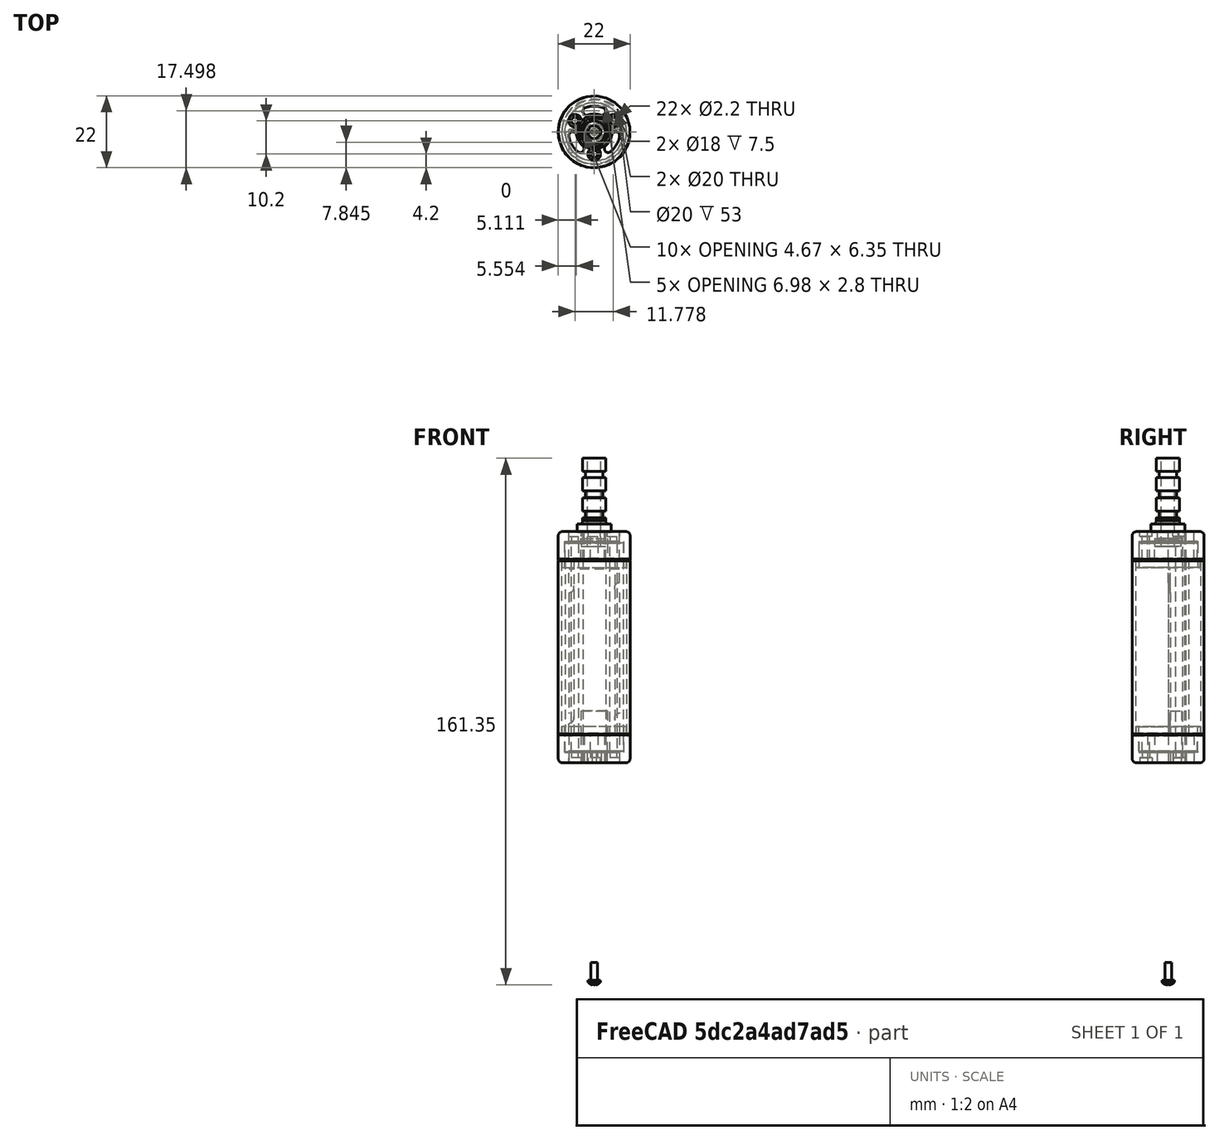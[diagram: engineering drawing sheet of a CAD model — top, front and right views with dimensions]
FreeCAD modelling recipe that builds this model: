
FCSTD DOCUMENT  (FreeCAD 1.1R44227 +568 (Git))
Label: Enclosure
License: All rights reserved
LicenseURL: http://en.wikipedia.org/wiki/All_rights_reserved
objects: Sketcher::SketchObject×40, PartDesign::Pocket×28, PartDesign::Pad×16, App::Point×15, PartDesign::Body×14, PartDesign::Fillet×12, App::FeaturePython×12, PartDesign::SubShapeBinder×9, App::Link×6, PartDesign::Plane×2, PartDesign::Revolution×2, Assembly::JointGroup×1, Assembly::ViewGroup×1, Assembly::AssemblyObject×1
note: 279 computed .brp shape members not serialized (recipe doc carries the construction recipe); baked Part::Feature solids carry a one-line shape summary decoded from their .brp

FEATURE [Sketcher::SketchObject] Sketch  label="22mmCircle"
  ArcFitTolerance = 1e-06
  AttachmentSupport = -> [XY_Plane]
  ExternalTypes = [0]
  FullyConstrained = true
  MakeInternals = false
  MapMode = 5
  _ExternalGeoVersion = 0
  sketch-geometry (1):
    g0: Circle CenterX=0 CenterY=0 CenterZ=0 NormalX=0 NormalY=0 NormalZ=1 AngleXU=0 Radius=11
  constraints (2):
    c: Diameter(g0) = 22
    c: Coincident(g0,g-1)
FEATURE [PartDesign::Pad] Pad
  Direction = (0,0,1)
  Length = 8.5
  Length2 = 10
  Profile = -> Sketch
  ReferenceAxis = -> Sketch [N_Axis]
  SideType = 0
  Suppressed = false
  Type = 0
  Type2 = 0
FEATURE [Sketcher::SketchObject] Sketch001
  ArcFitTolerance = 1e-06
  AttachmentSupport = -> [Pad]
  ExternalTypes = [0]
  FullyConstrained = true
  MakeInternals = false
  MapMode = 5
  Placement = pos=(0,0,8.5) rot=(0,0,1;0rad)
  _ExternalGeoVersion = 0
  sketch-geometry (1):
    g0: Circle CenterX=0 CenterY=0 CenterZ=0 NormalX=0 NormalY=0 NormalZ=1 AngleXU=0 Radius=9.85
  constraints (2):
    c: Diameter(g0) = 19.7
    c: Coincident(g0,g-1)
FEATURE [PartDesign::Pad] Pad001
  BaseFeature = -> Pad
  Direction = (0,0,1)
  Length = 2.5
  Length2 = 10
  Profile = -> Sketch001
  ReferenceAxis = -> Sketch001 [N_Axis]
  SideType = 0
  Suppressed = false
  Type = 0
  Type2 = 0
FEATURE [Sketcher::SketchObject] Sketch002
  ArcFitTolerance = 1e-06
  AttachmentSupport = -> [Pad001]
  ExternalTypes = [0]
  FullyConstrained = true
  MakeInternals = false
  MapMode = 5
  Placement = pos=(0,0,11) rot=(0,0,1;0rad)
  _ExternalGeoVersion = 0
  sketch-geometry (1):
    g0: Circle CenterX=0 CenterY=0 CenterZ=0 NormalX=0 NormalY=0 NormalZ=1 AngleXU=0 Radius=9
  constraints (2):
    c: Diameter(g0) = 18
    c: Coincident(g0,g-1)
FEATURE [PartDesign::Pocket] Pocket
  BaseFeature = -> Pad001
  Direction = (0,0,-1)
  Length = 7.5
  Length2 = 5
  Profile = -> Sketch002
  ReferenceAxis = -> Sketch002 [N_Axis]
  SideType = 0
  Suppressed = false
  Type = 0
  Type2 = 0
FEATURE [Sketcher::SketchObject] Sketch003  label="BoltHoles_outer"
  ArcFitTolerance = 1e-06
  AttachmentSupport = -> [Pocket]
  ExternalGeometry = -> [Pocket]
  ExternalTypes = [0]
  FullyConstrained = true
  MakeInternals = false
  MapMode = 5
  Placement = pos=(0,0,0) rot=(1,0,0;3.14159rad)
  _ExternalGeoVersion = 0
  sketch-geometry (5):
    g0: Circle CenterX=0 CenterY=6.8 CenterZ=0 NormalX=0 NormalY=0 NormalZ=1 AngleXU=0 Radius=1.95
    g1: Circle CenterX=-5.88897 CenterY=-3.4 CenterZ=0 NormalX=0 NormalY=0 NormalZ=1 AngleXU=0 Radius=1.95
    g2: Circle CenterX=5.88897 CenterY=-3.4 CenterZ=0 NormalX=0 NormalY=0 NormalZ=1 AngleXU=0 Radius=1.95
    g3: LineSegment [constr] StartX=0 StartY=0 StartZ=0 EndX=5.88897 EndY=-3.4 EndZ=0
    g4: LineSegment [constr] StartX=-5.88897 StartY=-3.4 StartZ=0 EndX=0 EndY=0 EndZ=0
  constraints (13):
    c: Diameter(g0) = 3.9
    c: PointOnObject(g0,g-2)
    c: Diameter(g1) = 3.9
    c: Diameter(g2) = 3.9
    c: Distance(g-1,g0) = 6.8
    c: Distance(g-1,g1) = 6.8
    c: Distance(g-1,g2) = 6.8
    c: Coincident(g3,g-1)
    c: Coincident(g3,g2)
    c: Angle(g3,g-2) = 2.0944
    c: Coincident(g4,g1)
    c: Coincident(g4,g3)
    c: Angle(g-2,g4) = 2.0944
FEATURE [PartDesign::Pocket] Pocket001
  BaseFeature = -> Pocket
  Direction = (0,0,1)
  Length = 1.5
  Length2 = 5
  Profile = -> Sketch003
  ReferenceAxis = -> Sketch003 [N_Axis]
  SideType = 0
  Suppressed = false
  Type = 0
  Type2 = 0
FEATURE [PartDesign::Fillet] Fillet
  Base = -> Pocket001 [Edge2]
  BaseFeature = -> Pocket001
  Radius = 1.2
  SupportTransform = false
  Suppressed = false
  UseAllEdges = false
FEATURE [Sketcher::SketchObject] Sketch005  label="BoltHoles_inner"
  ArcFitTolerance = 1e-06
  AttachmentSupport = -> [Fillet]
  ExternalGeometry = -> [Fillet]
  ExternalTypes = [0]
  FullyConstrained = true
  MakeInternals = false
  MapMode = 5
  Placement = pos=(0,0,1.5) rot=(1,0,0;3.14159rad)
  _ExternalGeoVersion = 0
  sketch-geometry (3):
    g0: Circle CenterX=-5.88897 CenterY=-3.4 CenterZ=0 NormalX=0 NormalY=0 NormalZ=1 AngleXU=0 Radius=1.1
    g1: Circle CenterX=0 CenterY=6.8 CenterZ=0 NormalX=0 NormalY=0 NormalZ=1 AngleXU=0 Radius=1.1
    g2: Circle CenterX=5.88897 CenterY=-3.4 CenterZ=0 NormalX=0 NormalY=0 NormalZ=1 AngleXU=0 Radius=1.1
  constraints (6):
    c: Diameter(g0) = 2.2
    c: Coincident(g0,g-4)
    c: Diameter(g1) = 2.2
    c: Coincident(g1,g-3)
    c: Diameter(g2) = 2.2
    c: Coincident(g2,g-5)
FEATURE [PartDesign::Pocket] Pocket002
  BaseFeature = -> Fillet
  Direction = (0,0,1)
  Length = 2
  Length2 = 5
  Profile = -> Sketch005
  ReferenceAxis = -> Sketch005 [N_Axis]
  SideType = 0
  Suppressed = false
  Type = 0
  Type2 = 0
FEATURE [Sketcher::SketchObject] Sketch006
  ArcFitTolerance = 1e-06
  AttachmentSupport = -> [XY_Plane001]
  ExternalTypes = [0]
  FullyConstrained = true
  MakeInternals = false
  MapMode = 5
  _ExternalGeoVersion = 0
  sketch-geometry (2):
    g0: Circle CenterX=0 CenterY=0 CenterZ=0 NormalX=0 NormalY=0 NormalZ=1 AngleXU=0 Radius=11
    g1: Circle CenterX=0 CenterY=0 CenterZ=0 NormalX=0 NormalY=0 NormalZ=1 AngleXU=0 Radius=10
  constraints (4):
    c: Diameter(g0) = 22
    c: Coincident(g0,g-1)
    c: Diameter(g1) = 20
    c: Coincident(g1,g0)
FEATURE [PartDesign::Pad] Pad002
  Direction = (0,0,1)
  Length = 53
  Length2 = 10
  Profile = -> Sketch006
  ReferenceAxis = -> Sketch006 [N_Axis]
  SideType = 0
  Suppressed = false
  Type = 0
  Type2 = 0
FEATURE [PartDesign::Body] Body001  label="QuartzTube"
  AllowCompound = false
  Group = -> [Sketch006,Pad002]
  Origin = -> Origin001
  Placement = pos=(0,0,77) rot=(0,0,1;0rad)
  Tip = -> Pad002
FEATURE [Sketcher::SketchObject] Sketch007  label="VentHoles"
  ArcFitTolerance = 1e-06
  AttachmentSupport = -> [Pocket002]
  ExternalGeometry = -> [Pocket002]
  ExternalTypes = [0]
  FullyConstrained = true
  MakeInternals = false
  MapMode = 5
  Placement = pos=(0,0,0) rot=(1,0,0;3.14159rad)
  _ExternalGeoVersion = 0
  sketch-geometry (58):
    g0: Circle [constr] CenterX=0 CenterY=0 CenterZ=0 NormalX=0 NormalY=0 NormalZ=1 AngleXU=0 Radius=7.9
    g1: Circle [constr] CenterX=0 CenterY=0 CenterZ=0 NormalX=0 NormalY=0 NormalZ=1 AngleXU=0 Radius=5.5
    g2: Circle [constr] CenterX=0 CenterY=0 CenterZ=0 NormalX=0 NormalY=0 NormalZ=1 AngleXU=0 Radius=4
    g3: Circle [constr] CenterX=0 CenterY=0 CenterZ=0 NormalX=0 NormalY=0 NormalZ=1 AngleXU=0 Radius=1.6
    g4: LineSegment [constr] StartX=0 StartY=0 StartZ=0 EndX=-6.29932 EndY=7.50724 EndZ=0
    g5: LineSegment [constr] StartX=0 StartY=0 StartZ=0 EndX=-9.65112 EndY=1.70175 EndZ=0
    g6: GeomPoint X=-5.07802 Y=6.05175 Z=0
    g7: GeomPoint X=-3.53533 Y=4.21324 Z=0
    g8: ArcOfCircle CenterX=-4.30668 CenterY=5.1325 CenterZ=0 NormalX=0 NormalY=0 NormalZ=1 AngleXU=0 Radius=1.2 StartAngle=5.41052 EndAngle=8.55211
    g9: GeomPoint X=-7.77998 Y=1.37182 Z=0
    g10: GeomPoint X=-5.41644 Y=0.955065 Z=0
    g11: ArcOfCircle CenterX=-6.59821 CenterY=1.16344 CenterZ=0 NormalX=0 NormalY=0 NormalZ=1 AngleXU=0 Radius=1.2 StartAngle=2.96706 EndAngle=6.10865
    g12: ArcOfCircle CenterX=0 CenterY=0 CenterZ=0 NormalX=0 NormalY=0 NormalZ=1 AngleXU=0 Radius=7.9 StartAngle=2.26893 EndAngle=2.96706
    g13: ArcOfCircle CenterX=-3e-16 CenterY=1e-16 CenterZ=0 NormalX=0 NormalY=0 NormalZ=1 AngleXU=0 Radius=5.5 StartAngle=2.26893 EndAngle=2.96706
    g14: LineSegment [constr] StartX=0 StartY=0 StartZ=0 EndX=6.29932 EndY=7.50724 EndZ=0
    g15: LineSegment [constr] StartX=-3e-16 StartY=1e-16 StartZ=0 EndX=9.65112 EndY=1.70175 EndZ=0
    g16: LineSegment [constr] StartX=0 StartY=0 StartZ=0 EndX=3.3518 EndY=-9.20899 EndZ=0
    g17: LineSegment [constr] StartX=0 StartY=0 StartZ=0 EndX=-3.3518 EndY=-9.20899 EndZ=0
    g18: GeomPoint X=5.07802 Y=6.05175 Z=0
    g19: GeomPoint X=3.53533 Y=4.21324 Z=0
    g20: GeomPoint X=5.41644 Y=0.955065 Z=0
    g21: GeomPoint X=7.77998 Y=1.37182 Z=0
    g22: GeomPoint X=-1.88111 Y=-5.16831 Z=0
    g23: GeomPoint X=-2.70196 Y=-7.42357 Z=0
    g24: GeomPoint X=1.88111 Y=-5.16831 Z=0
    g25: GeomPoint X=2.70196 Y=-7.42357 Z=0
    g26: ArcOfCircle CenterX=4.30668 CenterY=5.1325 CenterZ=0 NormalX=0 NormalY=0 NormalZ=1 AngleXU=0 Radius=1.2 StartAngle=0.872665 EndAngle=4.01426
    g27: ArcOfCircle CenterX=6.59821 CenterY=1.16344 CenterZ=0 NormalX=0 NormalY=0 NormalZ=1 AngleXU=0 Radius=1.2 StartAngle=3.31613 EndAngle=6.45772
    g28: ArcOfCircle CenterX=-3e-16 CenterY=0 CenterZ=0 NormalX=0 NormalY=0 NormalZ=1 AngleXU=0 Radius=7.9 StartAngle=0.174533 EndAngle=0.872665
    g29: ArcOfCircle CenterX=-1e-16 CenterY=9e-16 CenterZ=0 NormalX=0 NormalY=0 NormalZ=1 AngleXU=0 Radius=5.5 StartAngle=0.174533 EndAngle=0.872665
    g30: ArcOfCircle CenterX=-2.29153 CenterY=-6.29594 CenterZ=0 NormalX=0 NormalY=0 NormalZ=1 AngleXU=0 Radius=1.2 StartAngle=1.22173 EndAngle=4.36332
    g31: ArcOfCircle CenterX=2.29153 CenterY=-6.29594 CenterZ=0 NormalX=0 NormalY=0 NormalZ=1 AngleXU=0 Radius=1.2 StartAngle=5.06145 EndAngle=8.20305
    g32: ArcOfCircle CenterX=-1.5e-15 CenterY=2e-16 CenterZ=0 NormalX=0 NormalY=0 NormalZ=1 AngleXU=0 Radius=7.9 StartAngle=4.36332 EndAngle=5.06145
    g33: ArcOfCircle CenterX=-2e-16 CenterY=-2e-16 CenterZ=0 NormalX=0 NormalY=0 NormalZ=1 AngleXU=0 Radius=5.5 StartAngle=4.36332 EndAngle=5.06145
    g34: GeomPoint X=-2.57115 Y=3.06418 Z=0
    g35: GeomPoint X=-1.02846 Y=1.22567 Z=0
    g36: GeomPoint X=-3.93923 Y=0.694593 Z=0
    g37: GeomPoint X=-1.57569 Y=0.277837 Z=0
    g38: ArcOfCircle CenterX=-1.79981 CenterY=2.14492 CenterZ=0 NormalX=0 NormalY=0 NormalZ=1 AngleXU=0 Radius=1.2 StartAngle=5.41052 EndAngle=8.55211
    g39: ArcOfCircle CenterX=-2.75746 CenterY=0.486215 CenterZ=0 NormalX=0 NormalY=0 NormalZ=1 AngleXU=0 Radius=1.2 StartAngle=2.96706 EndAngle=6.10865
    g40: ArcOfCircle CenterX=-6e-16 CenterY=-4e-16 CenterZ=0 NormalX=0 NormalY=0 NormalZ=1 AngleXU=0 Radius=4 StartAngle=2.26893 EndAngle=2.96706
    g41: ArcOfCircle CenterX=1e-16 CenterY=1e-16 CenterZ=0 NormalX=0 NormalY=0 NormalZ=1 AngleXU=0 Radius=1.6 StartAngle=2.26893 EndAngle=2.96706
    g42: GeomPoint X=1.02846 Y=1.22567 Z=0
    g43: GeomPoint X=2.57115 Y=3.06418 Z=0
    g44: GeomPoint X=1.57569 Y=0.277837 Z=0
    g45: GeomPoint X=3.93923 Y=0.694593 Z=0
    g46: GeomPoint X=1.36808 Y=-3.75877 Z=0
    g47: GeomPoint X=0.547232 Y=-1.50351 Z=0
    g48: GeomPoint X=-1.36808 Y=-3.75877 Z=0
    g49: GeomPoint X=-0.547232 Y=-1.50351 Z=0
    g50: ArcOfCircle CenterX=0 CenterY=0 CenterZ=0 NormalX=0 NormalY=0 NormalZ=1 AngleXU=0 Radius=1.6 StartAngle=4.36332 EndAngle=5.06145
    g51: ArcOfCircle CenterX=-3e-16 CenterY=-4e-16 CenterZ=0 NormalX=0 NormalY=0 NormalZ=1 AngleXU=0 Radius=4 StartAngle=4.36332 EndAngle=5.06145
    g52: ArcOfCircle CenterX=0.957656 CenterY=-2.63114 CenterZ=0 NormalX=0 NormalY=0 NormalZ=1 AngleXU=0 Radius=1.2 StartAngle=5.06145 EndAngle=8.20305
    g53: ArcOfCircle CenterX=-0.957656 CenterY=-2.63114 CenterZ=0 NormalX=0 NormalY=0 NormalZ=1 AngleXU=0 Radius=1.2 StartAngle=1.22173 EndAngle=4.36332
    g54: ArcOfCircle CenterX=1.79981 CenterY=2.14492 CenterZ=0 NormalX=0 NormalY=0 NormalZ=1 AngleXU=0 Radius=1.2 StartAngle=0.872665 EndAngle=4.01426
    g55: ArcOfCircle CenterX=2.75746 CenterY=0.486215 CenterZ=0 NormalX=0 NormalY=0 NormalZ=1 AngleXU=0 Radius=1.2 StartAngle=3.31613 EndAngle=6.45772
    g56: ArcOfCircle CenterX=1e-16 CenterY=1e-16 CenterZ=0 NormalX=0 NormalY=0 NormalZ=1 AngleXU=0 Radius=1.6 StartAngle=0.174533 EndAngle=0.872665
    g57: ArcOfCircle CenterX=-1.6749e-12 CenterY=-9.675e-13 CenterZ=0 NormalX=0 NormalY=0 NormalZ=1 AngleXU=0 Radius=4 StartAngle=0.174533 EndAngle=0.872665
  constraints (146):
    c: Diameter(g0) = 15.8
    c: Coincident(g0,g-1)
    c: Diameter(g1) = 11
    c: Coincident(g1,g0)
    c: Diameter(g2) = 8
    c: Coincident(g2,g0)
    c: Diameter(g3) = 3.2
    c: Coincident(g3,g0)
    c: Coincident(g4,g0)
    c: PointOnObject(g4,g-3)
    c: Angle(g-2,g4) = 0.698132
    c: Coincident(g5,g0)
    c: PointOnObject(g5,g-3)
    c: Angle(g4,g5) = 0.698132
    c: PointOnObject(g6,g0)
    c: PointOnObject(g6,g4)
    c: PointOnObject(g7,g1)
    c: PointOnObject(g7,g4)
    c: Coincident(g8,g6)
    c: Coincident(g8,g7)
    c: PointOnObject(g8,g4)
    c: PointOnObject(g9,g0)
    c: PointOnObject(g10,g1)
    c: PointOnObject(g10,g5)
    c: PointOnObject(g9,g5)
    c: Coincident(g11,g9)
    c: Coincident(g11,g10)
    c: PointOnObject(g11,g5)
    c: Equal(g0,g12)
    c: Coincident(g12,g6)
    c: Coincident(g12,g9)
    c: Equal(g13,g1)
    c: Coincident(g13,g7)
    c: Coincident(g13,g10)
    c: Coincident(g14,g12)
    c: PointOnObject(g14,g-3)
    c: Coincident(g15,g13)
    c: PointOnObject(g15,g-3)
    c: Angle(g14,g-2) = 0.698132
    c: Angle(g15,g14) = 0.698132
    c: Coincident(g16,g0)
    c: PointOnObject(g16,g-3)
    c: Coincident(g17,g0)
    c: PointOnObject(g17,g-3)
    c: Angle(g-2,g16) = 0.349066
    c: Angle(g17,g16) = 0.698132
    c: PointOnObject(g18,g14)
    c: PointOnObject(g19,g14)
    c: PointOnObject(g20,g15)
    c: PointOnObject(g21,g15)
    c: PointOnObject(g18,g0)
    c: PointOnObject(g19,g1)
    c: PointOnObject(g20,g1)
    c: PointOnObject(g21,g0)
    c: PointOnObject(g22,g17)
    c: PointOnObject(g23,g17)
    c: PointOnObject(g24,g16)
    c: PointOnObject(g25,g16)
    c: PointOnObject(g25,g0)
    c: PointOnObject(g24,g1)
    c: PointOnObject(g22,g1)
    c: PointOnObject(g23,g0)
    c: Coincident(g26,g18)
    c: Coincident(g26,g19)
    c: Coincident(g27,g20)
    c: Coincident(g27,g21)
    c: PointOnObject(g27,g15)
    c: PointOnObject(g26,g14)
    c: Coincident(g28,g18)
    c: Coincident(g28,g21)
    c: Equal(g0,g28)
    c: Coincident(g29,g19)
    c: Coincident(g29,g20)
    c: Equal(g29,g1)
    c: Coincident(g30,g22)
    c: Coincident(g30,g23)
    c: Coincident(g31,g25)
    c: Coincident(g31,g24)
    c: PointOnObject(g31,g16)
    c: PointOnObject(g30,g17)
    c: Coincident(g33,g24)
    c: Coincident(g33,g22)
    c: Coincident(g32,g23)
    c: Coincident(g32,g25)
    c: Equal(g33,g1)
    c: Equal(g32,g0)
    c: PointOnObject(g34,g4)
    c: PointOnObject(g35,g4)
    c: PointOnObject(g36,g5)
    c: PointOnObject(g37,g5)
    c: PointOnObject(g34,g2)
    c: PointOnObject(g35,g3)
    c: PointOnObject(g37,g3)
    c: PointOnObject(g36,g2)
    c: Coincident(g38,g35)
    c: Coincident(g38,g34)
    c: Coincident(g39,g37)
    c: Coincident(g39,g36)
    c: PointOnObject(g39,g5)
    c: PointOnObject(g38,g4)
    c: Coincident(g41,g35)
    c: Coincident(g41,g37)
    c: Coincident(g40,g34)
    c: Coincident(g40,g36)
    c: Equal(g40,g2)
    c: Equal(g41,g3)
    c: PointOnObject(g42,g14)
    c: PointOnObject(g43,g14)
    c: PointOnObject(g44,g15)
    c: PointOnObject(g45,g15)
    c: PointOnObject(g46,g16)
    c: PointOnObject(g47,g16)
    c: PointOnObject(g48,g17)
    c: PointOnObject(g49,g17)
    c: PointOnObject(g47,g3)
    c: PointOnObject(g46,g2)
    c: PointOnObject(g48,g2)
    c: PointOnObject(g49,g3)
    c: PointOnObject(g45,g2)
    c: PointOnObject(g43,g2)
    c: PointOnObject(g42,g3)
    c: PointOnObject(g44,g3)
    c: Coincident(g51,g46)
    c: Coincident(g51,g48)
    c: Coincident(g50,g49)
    c: Coincident(g47,g50)
    c: Equal(g51,g2)
    c: Equal(g50,g3)
    c: Coincident(g52,g47)
    c: Coincident(g52,g46)
    c: Coincident(g53,g48)
    c: Coincident(g53,g49)
    c: PointOnObject(g53,g17)
    c: PointOnObject(g52,g16)
    c: Coincident(g54,g42)
    c: Coincident(g54,g43)
    c: Coincident(g55,g44)
    c: Coincident(g55,g45)
    c: PointOnObject(g55,g15)
    c: PointOnObject(g54,g14)
    c: Coincident(g42,g56)
    c: Coincident(g56,g44)
    c: Coincident(g57,g43)
    c: Coincident(g57,g45)
    c: Equal(g56,g3)
    c: Equal(g57,g2)
FEATURE [PartDesign::Pocket] Pocket003
  BaseFeature = -> Pocket002
  Direction = (0,0,1)
  Length = 3.5
  Length2 = 5
  Profile = -> Sketch007
  ReferenceAxis = -> Sketch007 [N_Axis]
  SideType = 0
  Suppressed = false
  Type = 0
  Type2 = 0
FEATURE [PartDesign::Body] Body  label="EndCap_Bottom"
  AllowCompound = false
  Group = -> [Sketch,Pad,Sketch001,Pad001,Sketch002,Pocket,Sketch003,Pocket001,Fillet,Sketch005,Pocket002,Sketch007,Pocket003]
  Origin = -> Origin
  Placement = pos=(0,1e-05,68.2) rot=(0,0,1;0rad)
  Tip = -> Pocket003
FEATURE [Sketcher::SketchObject] Sketch008  label="22mmCircle001"
  ArcFitTolerance = 1e-06
  AttachmentSupport = -> [XY_Plane002]
  ExternalTypes = [0]
  FullyConstrained = true
  MakeInternals = false
  MapMode = 5
  _ExternalGeoVersion = 0
  sketch-geometry (1):
    g0: Circle CenterX=0 CenterY=0 CenterZ=0 NormalX=0 NormalY=0 NormalZ=1 AngleXU=0 Radius=11
  constraints (2):
    c: Diameter(g0) = 22
    c: Coincident(g0,g-1)
FEATURE [PartDesign::Pad] Pad003
  Direction = (0,0,1)
  Length = 8.5
  Length2 = 10
  Profile = -> Sketch008
  ReferenceAxis = -> Sketch008 [N_Axis]
  SideType = 0
  Suppressed = false
  Type = 0
  Type2 = 0
FEATURE [Sketcher::SketchObject] Sketch009
  ArcFitTolerance = 1e-06
  AttachmentSupport = -> [Pad003]
  ExternalTypes = [0]
  FullyConstrained = true
  MakeInternals = false
  MapMode = 5
  Placement = pos=(0,0,8.5) rot=(0,0,1;0rad)
  _ExternalGeoVersion = 0
  sketch-geometry (1):
    g0: Circle CenterX=0 CenterY=0 CenterZ=0 NormalX=0 NormalY=0 NormalZ=1 AngleXU=0 Radius=9.85
  constraints (2):
    c: Diameter(g0) = 19.7
    c: Coincident(g0,g-1)
FEATURE [PartDesign::Pad] Pad004
  BaseFeature = -> Pad003
  Direction = (0,0,1)
  Length = 2.5
  Length2 = 10
  Profile = -> Sketch009
  ReferenceAxis = -> Sketch009 [N_Axis]
  SideType = 0
  Suppressed = false
  Type = 0
  Type2 = 0
FEATURE [Sketcher::SketchObject] Sketch010
  ArcFitTolerance = 1e-06
  AttachmentSupport = -> [Pad004]
  ExternalTypes = [0]
  FullyConstrained = true
  MakeInternals = false
  MapMode = 5
  Placement = pos=(0,0,11) rot=(0,0,1;0rad)
  _ExternalGeoVersion = 0
  sketch-geometry (1):
    g0: Circle CenterX=0 CenterY=0 CenterZ=0 NormalX=0 NormalY=0 NormalZ=1 AngleXU=0 Radius=9
  constraints (2):
    c: Diameter(g0) = 18
    c: Coincident(g0,g-1)
FEATURE [PartDesign::Pocket] Pocket004
  BaseFeature = -> Pad004
  Direction = (0,0,-1)
  Length = 7.5
  Length2 = 5
  Profile = -> Sketch010
  ReferenceAxis = -> Sketch010 [N_Axis]
  SideType = 0
  Suppressed = false
  Type = 0
  Type2 = 0
FEATURE [Sketcher::SketchObject] Sketch011  label="BoltHoles_outer001"
  ArcFitTolerance = 1e-06
  AttachmentSupport = -> [Pocket004]
  ExternalGeometry = -> [Pocket004]
  ExternalTypes = [0]
  FullyConstrained = true
  MakeInternals = false
  MapMode = 5
  Placement = pos=(0,0,0) rot=(1,0,0;3.14159rad)
  _ExternalGeoVersion = 0
  sketch-geometry (5):
    g0: Circle CenterX=0 CenterY=6.8 CenterZ=0 NormalX=0 NormalY=0 NormalZ=1 AngleXU=0 Radius=1.95
    g1: Circle CenterX=-5.88897 CenterY=-3.4 CenterZ=0 NormalX=0 NormalY=0 NormalZ=1 AngleXU=0 Radius=1.95
    g2: Circle CenterX=5.88897 CenterY=-3.4 CenterZ=0 NormalX=0 NormalY=0 NormalZ=1 AngleXU=0 Radius=1.95
    g3: LineSegment [constr] StartX=0 StartY=0 StartZ=0 EndX=5.88897 EndY=-3.4 EndZ=0
    g4: LineSegment [constr] StartX=-5.88897 StartY=-3.4 StartZ=0 EndX=0 EndY=0 EndZ=0
  constraints (13):
    c: Diameter(g0) = 3.9
    c: PointOnObject(g0,g-2)
    c: Diameter(g1) = 3.9
    c: Diameter(g2) = 3.9
    c: Distance(g-1,g0) = 6.8
    c: Distance(g-1,g1) = 6.8
    c: Distance(g-1,g2) = 6.8
    c: Coincident(g3,g-1)
    c: Coincident(g3,g2)
    c: Angle(g3,g-2) = 2.0944
    c: Coincident(g4,g1)
    c: Coincident(g4,g3)
    c: Angle(g-2,g4) = 2.0944
FEATURE [PartDesign::Pocket] Pocket005
  BaseFeature = -> Pocket004
  Direction = (0,0,1)
  Length = 1.5
  Length2 = 5
  Profile = -> Sketch011
  ReferenceAxis = -> Sketch011 [N_Axis]
  SideType = 0
  Suppressed = false
  Type = 0
  Type2 = 0
FEATURE [PartDesign::Fillet] Fillet001
  Base = -> Pocket005 [Edge2]
  BaseFeature = -> Pocket005
  Radius = 1.2
  SupportTransform = false
  Suppressed = false
  UseAllEdges = false
FEATURE [Sketcher::SketchObject] Sketch012  label="BoltHoles_inner001"
  ArcFitTolerance = 1e-06
  AttachmentSupport = -> [Fillet001]
  ExternalGeometry = -> [Fillet001]
  ExternalTypes = [0]
  FullyConstrained = true
  MakeInternals = false
  MapMode = 5
  Placement = pos=(0,0,1.5) rot=(1,0,0;3.14159rad)
  _ExternalGeoVersion = 0
  sketch-geometry (3):
    g0: Circle CenterX=-5.88897 CenterY=-3.4 CenterZ=0 NormalX=0 NormalY=0 NormalZ=1 AngleXU=0 Radius=1.1
    g1: Circle CenterX=0 CenterY=6.8 CenterZ=0 NormalX=0 NormalY=0 NormalZ=1 AngleXU=0 Radius=1.1
    g2: Circle CenterX=5.88897 CenterY=-3.4 CenterZ=0 NormalX=0 NormalY=0 NormalZ=1 AngleXU=0 Radius=1.1
  constraints (6):
    c: Diameter(g0) = 2.2
    c: Coincident(g0,g-4)
    c: Diameter(g1) = 2.2
    c: Coincident(g1,g-3)
    c: Diameter(g2) = 2.2
    c: Coincident(g2,g-5)
FEATURE [PartDesign::Pocket] Pocket006
  BaseFeature = -> Fillet001
  Direction = (0,0,1)
  Length = 2
  Length2 = 5
  Profile = -> Sketch012
  ReferenceAxis = -> Sketch012 [N_Axis]
  SideType = 0
  Suppressed = false
  Type = 0
  Type2 = 0
FEATURE [Sketcher::SketchObject] Sketch013  label="VentHoles001"
  ArcFitTolerance = 1e-06
  AttachmentSupport = -> [Pocket006]
  ExternalGeometry = -> [Pocket006]
  ExternalTypes = [0]
  FullyConstrained = true
  MakeInternals = false
  MapMode = 5
  Placement = pos=(0,0,0) rot=(1,0,0;3.14159rad)
  _ExternalGeoVersion = 0
  sketch-geometry (33):
    g0: Circle [constr] CenterX=0 CenterY=0 CenterZ=0 NormalX=0 NormalY=0 NormalZ=1 AngleXU=0 Radius=7.9
    g1: Circle [constr] CenterX=0 CenterY=0 CenterZ=0 NormalX=0 NormalY=0 NormalZ=1 AngleXU=0 Radius=5.5
    g2: Circle CenterX=0 CenterY=0 CenterZ=0 NormalX=0 NormalY=0 NormalZ=1 AngleXU=0 Radius=3.3
    g3: LineSegment [constr] StartX=0 StartY=0 StartZ=0 EndX=-6.29932 EndY=7.50724 EndZ=0
    g4: LineSegment [constr] StartX=0 StartY=0 StartZ=0 EndX=-9.65112 EndY=1.70175 EndZ=0
    g5: GeomPoint X=-5.07802 Y=6.05175 Z=0
    g6: GeomPoint X=-3.53533 Y=4.21324 Z=0
    g7: ArcOfCircle CenterX=-4.30668 CenterY=5.1325 CenterZ=0 NormalX=0 NormalY=0 NormalZ=1 AngleXU=0 Radius=1.2 StartAngle=5.41052 EndAngle=8.55211
    g8: GeomPoint X=-7.77998 Y=1.37182 Z=0
    g9: GeomPoint X=-5.41644 Y=0.955065 Z=0
    g10: ArcOfCircle CenterX=-6.59821 CenterY=1.16344 CenterZ=0 NormalX=0 NormalY=0 NormalZ=1 AngleXU=0 Radius=1.2 StartAngle=2.96706 EndAngle=6.10865
    g11: ArcOfCircle CenterX=4e-16 CenterY=-2e-16 CenterZ=0 NormalX=0 NormalY=0 NormalZ=1 AngleXU=0 Radius=7.9 StartAngle=2.26893 EndAngle=2.96706
    g12: ArcOfCircle CenterX=-3e-16 CenterY=-2e-16 CenterZ=0 NormalX=0 NormalY=0 NormalZ=1 AngleXU=0 Radius=5.5 StartAngle=2.26893 EndAngle=2.96706
    g13: LineSegment [constr] StartX=4e-16 StartY=-2e-16 StartZ=0 EndX=6.29932 EndY=7.50724 EndZ=0
    g14: LineSegment [constr] StartX=-3e-16 StartY=-2e-16 StartZ=0 EndX=9.65112 EndY=1.70175 EndZ=0
    g15: LineSegment [constr] StartX=0 StartY=0 StartZ=0 EndX=3.3518 EndY=-9.20899 EndZ=0
    g16: LineSegment [constr] StartX=0 StartY=0 StartZ=0 EndX=-3.3518 EndY=-9.20899 EndZ=0
    g17: GeomPoint X=5.07802 Y=6.05175 Z=0
    g18: GeomPoint X=3.53533 Y=4.21324 Z=0
    g19: GeomPoint X=5.41644 Y=0.955065 Z=0
    g20: GeomPoint X=7.77998 Y=1.37182 Z=0
    g21: GeomPoint X=-1.88111 Y=-5.16831 Z=0
    g22: GeomPoint X=-2.70196 Y=-7.42357 Z=0
    g23: GeomPoint X=1.88111 Y=-5.16831 Z=0
    g24: GeomPoint X=2.70196 Y=-7.42357 Z=0
    g25: ArcOfCircle CenterX=4.30668 CenterY=5.1325 CenterZ=0 NormalX=0 NormalY=0 NormalZ=1 AngleXU=0 Radius=1.2 StartAngle=0.872665 EndAngle=4.01426
    g26: ArcOfCircle CenterX=6.59821 CenterY=1.16344 CenterZ=0 NormalX=0 NormalY=0 NormalZ=1 AngleXU=0 Radius=1.2 StartAngle=3.31613 EndAngle=6.45772
    g27: ArcOfCircle CenterX=0 CenterY=0 CenterZ=0 NormalX=0 NormalY=0 NormalZ=1 AngleXU=0 Radius=7.9 StartAngle=0.174533 EndAngle=0.872665
    g28: ArcOfCircle CenterX=2e-16 CenterY=3e-16 CenterZ=0 NormalX=0 NormalY=0 NormalZ=1 AngleXU=0 Radius=5.5 StartAngle=0.174533 EndAngle=0.872665
    g29: ArcOfCircle CenterX=-2.29153 CenterY=-6.29594 CenterZ=0 NormalX=0 NormalY=0 NormalZ=1 AngleXU=0 Radius=1.2 StartAngle=1.22173 EndAngle=4.36332
    g30: ArcOfCircle CenterX=2.29153 CenterY=-6.29594 CenterZ=0 NormalX=0 NormalY=0 NormalZ=1 AngleXU=0 Radius=1.2 StartAngle=5.06145 EndAngle=8.20305
    g31: ArcOfCircle CenterX=-8e-16 CenterY=1.1e-15 CenterZ=0 NormalX=0 NormalY=0 NormalZ=1 AngleXU=0 Radius=7.9 StartAngle=4.36332 EndAngle=5.06145
    g32: ArcOfCircle CenterX=-2.6e-15 CenterY=1e-16 CenterZ=0 NormalX=0 NormalY=0 NormalZ=1 AngleXU=0 Radius=5.5 StartAngle=4.36332 EndAngle=5.06145
  constraints (84):
    c: Diameter(g0) = 15.8
    c: Coincident(g0,g-1)
    c: Diameter(g1) = 11
    c: Coincident(g1,g0)
    c: Diameter(g2) = 6.6
    c: Coincident(g2,g0)
    c: Coincident(g3,g0)
    c: PointOnObject(g3,g-3)
    c: Angle(g-2,g3) = 0.698132
    c: Coincident(g4,g0)
    c: PointOnObject(g4,g-3)
    c: Angle(g3,g4) = 0.698132
    c: PointOnObject(g5,g0)
    c: PointOnObject(g5,g3)
    c: PointOnObject(g6,g1)
    c: PointOnObject(g6,g3)
    c: Coincident(g7,g5)
    c: Coincident(g7,g6)
    c: PointOnObject(g7,g3)
    c: PointOnObject(g8,g0)
    c: PointOnObject(g9,g1)
    c: PointOnObject(g9,g4)
    c: PointOnObject(g8,g4)
    c: Coincident(g10,g8)
    c: Coincident(g10,g9)
    c: PointOnObject(g10,g4)
    c: Equal(g0,g11)
    c: Coincident(g11,g5)
    c: Coincident(g11,g8)
    c: Equal(g12,g1)
    c: Coincident(g12,g6)
    c: Coincident(g12,g9)
    c: Coincident(g13,g11)
    c: PointOnObject(g13,g-3)
    c: Coincident(g14,g12)
    c: PointOnObject(g14,g-3)
    c: Angle(g13,g-2) = 0.698132
    c: Angle(g14,g13) = 0.698132
    c: Coincident(g15,g0)
    c: PointOnObject(g15,g-3)
    c: Coincident(g16,g0)
    c: PointOnObject(g16,g-3)
    c: Angle(g-2,g15) = 0.349066
    c: Angle(g16,g15) = 0.698132
    c: PointOnObject(g17,g13)
    c: PointOnObject(g18,g13)
    c: PointOnObject(g19,g14)
    c: PointOnObject(g20,g14)
    c: PointOnObject(g17,g0)
    c: PointOnObject(g18,g1)
    c: PointOnObject(g19,g1)
    c: PointOnObject(g20,g0)
    c: PointOnObject(g21,g16)
    c: PointOnObject(g22,g16)
    c: PointOnObject(g23,g15)
    c: PointOnObject(g24,g15)
    c: PointOnObject(g24,g0)
    c: PointOnObject(g23,g1)
    c: PointOnObject(g21,g1)
    c: PointOnObject(g22,g0)
    c: Coincident(g25,g17)
    c: Coincident(g25,g18)
    c: Coincident(g26,g19)
    c: Coincident(g26,g20)
    c: PointOnObject(g26,g14)
    c: PointOnObject(g25,g13)
    c: Coincident(g27,g17)
    c: Coincident(g27,g20)
    c: Equal(g0,g27)
    c: Coincident(g28,g18)
    c: Coincident(g28,g19)
    c: Equal(g28,g1)
    c: Coincident(g29,g21)
    c: Coincident(g29,g22)
    c: Coincident(g30,g24)
    c: Coincident(g30,g23)
    c: PointOnObject(g30,g15)
    c: PointOnObject(g29,g16)
    c: Coincident(g32,g23)
    c: Coincident(g32,g21)
    c: Coincident(g31,g22)
    c: Coincident(g31,g24)
    c: Equal(g32,g1)
    c: Equal(g31,g0)
FEATURE [PartDesign::Pocket] Pocket007
  BaseFeature = -> Pocket006
  Direction = (0,0,1)
  Length = 3.5
  Length2 = 5
  Profile = -> Sketch013
  ReferenceAxis = -> Sketch013 [N_Axis]
  SideType = 0
  Suppressed = false
  Type = 0
  Type2 = 0
FEATURE [Sketcher::SketchObject] Sketch014
  ArcFitTolerance = 1e-06
  AttachmentSupport = -> [Pocket007]
  ExternalTypes = [0]
  FullyConstrained = true
  MakeInternals = false
  MapMode = 5
  Placement = pos=(0,0,3.5) rot=(0,0,1;0rad)
  _ExternalGeoVersion = 0
  sketch-geometry (1):
    g0: Circle CenterX=0 CenterY=0 CenterZ=0 NormalX=0 NormalY=0 NormalZ=1 AngleXU=0 Radius=4.1
  constraints (2):
    c: Diameter(g0) = 8.2
    c: Coincident(g0,g-1)
FEATURE [PartDesign::Pocket] Pocket008
  BaseFeature = -> Pocket007
  Direction = (0,0,-1)
  Length = 1.4
  Length2 = 5
  Profile = -> Sketch014
  ReferenceAxis = -> Sketch014 [N_Axis]
  SideType = 0
  Suppressed = false
  Type = 0
  Type2 = 0
FEATURE [PartDesign::Body] Body002  label="EndCap_Top"
  AllowCompound = false
  Group = -> [Sketch008,Pad003,Sketch009,Pad004,Sketch010,Pocket004,Sketch011,Pocket005,Fillet001,Sketch012,Pocket006,Sketch013,Pocket007,Sketch014,Pocket008]
  Origin = -> Origin002
  Placement = pos=(2.39184e-06,1e-05,139) rot=(0,1.00436,0;3.14159rad)
  Tip = -> Pocket008
FEATURE [Sketcher::SketchObject] Sketch016
  ArcFitTolerance = 1e-06
  AttachmentSupport = -> [XY_Plane004]
  ExternalTypes = [0]
  FullyConstrained = true
  MakeInternals = false
  MapMode = 5
  _ExternalGeoVersion = 0
  sketch-geometry (2):
    g0: Circle CenterX=0 CenterY=0 CenterZ=0 NormalX=0 NormalY=0 NormalZ=1 AngleXU=0 Radius=11
    g1: Circle CenterX=0 CenterY=0 CenterZ=0 NormalX=0 NormalY=0 NormalZ=1 AngleXU=0 Radius=10
  constraints (4):
    c: Diameter(g0) = 22
    c: Coincident(g0,g-1)
    c: Diameter(g1) = 20
    c: Coincident(g1,g0)
FEATURE [PartDesign::Pad] Pad006
  Direction = (0,0,1)
  Length = 0.75
  Length2 = 10
  Profile = -> Sketch016
  ReferenceAxis = -> Sketch016 [N_Axis]
  SideType = 0
  Suppressed = false
  Type = 0
  Type2 = 0
FEATURE [PartDesign::Fillet] Fillet002
  Base = -> Pad006 [Edge3]
  BaseFeature = -> Pad006
  Radius = 0.35
  SupportTransform = false
  Suppressed = false
  UseAllEdges = false
FEATURE [PartDesign::Fillet] Fillet003
  Base = -> Fillet002 [Edge3]
  BaseFeature = -> Fillet002
  Radius = 0.35
  SupportTransform = false
  Suppressed = false
  UseAllEdges = false
FEATURE [PartDesign::Fillet] Fillet004
  Base = -> Fillet003 [Edge9]
  BaseFeature = -> Fillet003
  Radius = 0.35
  SupportTransform = false
  Suppressed = false
  UseAllEdges = false
FEATURE [PartDesign::Fillet] Fillet005
  Base = -> Fillet004 [Edge8]
  BaseFeature = -> Fillet004
  Radius = 0.35
  SupportTransform = false
  Suppressed = false
  UseAllEdges = false
FEATURE [PartDesign::Body] Body004  label="RubberRing_Top"
  AllowCompound = false
  Group = -> [Sketch016,Pad006,Fillet002,Fillet003,Fillet004,Fillet005]
  Origin = -> Origin004
  Placement = pos=(0,-1e-05,130) rot=(0,0,1;0rad)
  Tip = -> Fillet005
FEATURE [Sketcher::SketchObject] Sketch017
  ArcFitTolerance = 1e-06
  AttachmentSupport = -> [XY_Plane005]
  ExternalTypes = [0]
  FullyConstrained = true
  MakeInternals = false
  MapMode = 5
  _ExternalGeoVersion = 0
  sketch-geometry (2):
    g0: Circle CenterX=0 CenterY=0 CenterZ=0 NormalX=0 NormalY=0 NormalZ=1 AngleXU=0 Radius=11
    g1: Circle CenterX=0 CenterY=0 CenterZ=0 NormalX=0 NormalY=0 NormalZ=1 AngleXU=0 Radius=10
  constraints (4):
    c: Diameter(g0) = 22
    c: Coincident(g0,g-1)
    c: Diameter(g1) = 20
    c: Coincident(g1,g0)
FEATURE [PartDesign::Pad] Pad007
  Direction = (0,0,1)
  Length = 0.75
  Length2 = 10
  Profile = -> Sketch017
  ReferenceAxis = -> Sketch017 [N_Axis]
  SideType = 0
  Suppressed = false
  Type = 0
  Type2 = 0
FEATURE [PartDesign::Fillet] Fillet006
  Base = -> Pad007 [Edge3]
  BaseFeature = -> Pad007
  Radius = 0.35
  SupportTransform = false
  Suppressed = false
  UseAllEdges = false
FEATURE [PartDesign::Fillet] Fillet007
  Base = -> Fillet006 [Edge3]
  BaseFeature = -> Fillet006
  Radius = 0.35
  SupportTransform = false
  Suppressed = false
  UseAllEdges = false
FEATURE [PartDesign::Fillet] Fillet008
  Base = -> Fillet007 [Edge9]
  BaseFeature = -> Fillet007
  Radius = 0.35
  SupportTransform = false
  Suppressed = false
  UseAllEdges = false
FEATURE [PartDesign::Fillet] Fillet009
  Base = -> Fillet008 [Edge8]
  BaseFeature = -> Fillet008
  Radius = 0.35
  SupportTransform = false
  Suppressed = false
  UseAllEdges = false
FEATURE [PartDesign::Body] Body005  label="RubberRing_Bottom"
  AllowCompound = false
  Group = -> [Sketch017,Pad007,Fillet006,Fillet007,Fillet008,Fillet009]
  Origin = -> Origin005
  Placement = pos=(0,1e-05,76.4) rot=(0,0,1;0rad)
  Tip = -> Fillet009
FEATURE [PartDesign::SubShapeBinder] Binder
  BindCopyOnChange = 0
  BindMode = 0
  ClaimChildren = false
  Context = -> Assembly [Body006.Binder.]
  Fuse = false
  MakeFace = true
  OffsetFill = false
  OffsetIntersection = false
  OffsetJoinType = 0
  OffsetOpenResult = false
  PartialLoad = false
  Relative = true
  Support = -> [Body002[Pocket008.Edge61,Pocket008.Edge58,Pocket008.Edge62,Pocket008.Edge60,Pocket008.Edge59]]
  _Version = 2
FEATURE [PartDesign::Pad] Pad008
  Direction = (0,0,1)
  Length = 0.25
  Length2 = 10
  Profile = -> Binder
  SideType = 0
  Suppressed = false
  Type = 0
  Type2 = 0
FEATURE [PartDesign::Body] Body006  label="Mesh_Top"
  AllowCompound = false
  Group = -> [Binder,Pad008]
  Origin = -> Origin006
  Placement = pos=(0,-1e-05,54.8001) rot=(0,0,1;0rad)
  Tip = -> Pad008
FEATURE [PartDesign::SubShapeBinder] Binder001
  BindCopyOnChange = 0
  BindMode = 0
  ClaimChildren = false
  Context = -> Assembly [Body007.Binder001.]
  Fuse = false
  MakeFace = true
  OffsetFill = false
  OffsetIntersection = false
  OffsetJoinType = 0
  OffsetOpenResult = false
  PartialLoad = false
  Relative = true
  Support = -> [Body[Pocket003.Edge91,Pocket003.Edge92,Pocket003.Edge94,Pocket003.Edge93]]
  _Version = 2
FEATURE [PartDesign::Pad] Pad009
  Direction = (0,0,1)
  Length = 0.1
  Length2 = 10
  Profile = -> Binder001
  SideType = 0
  Suppressed = false
  Type = 0
  Type2 = 0
FEATURE [PartDesign::Body] Body007  label="Mesh_Bottom"
  AllowCompound = false
  Group = -> [Binder001,Pad009]
  Origin = -> Origin007
  Placement = pos=(0,1e-05,110.8) rot=(0,0,1;0rad)
  Tip = -> Pad009
FEATURE [Assembly::JointGroup] Joints
FEATURE [PartDesign::SubShapeBinder] Binder002
  BindCopyOnChange = 0
  BindMode = 0
  ClaimChildren = false
  Context = -> Assembly [Body008.Binder002.]
  Fuse = false
  MakeFace = true
  OffsetFill = false
  OffsetIntersection = false
  OffsetJoinType = 0
  OffsetOpenResult = false
  PartialLoad = false
  Relative = true
  Support = -> [Body002[Pocket008.Edge58,Pocket008.Edge59,Pocket008.Edge60,Pocket008.Edge62]]
  _Version = 2
FEATURE [Sketcher::SketchObject] Sketch018
  ArcFitTolerance = 1e-06
  AttachmentSupport = -> [Binder002]
  ExternalGeometry = -> [Binder002]
  ExternalTypes = [0]
  FullyConstrained = true
  MakeInternals = false
  MapMode = 5
  Placement = pos=(1.7366e-05,0,99.5) rot=(0,1.00873,0;0rad)
  _ExternalGeoVersion = 0
  sketch-geometry (4):
    g0: Circle CenterX=0 CenterY=0 CenterZ=0 NormalX=0 NormalY=0 NormalZ=1 AngleXU=0 Radius=8.9
    g1: Circle CenterX=-5.88899 CenterY=3.40002 CenterZ=0 NormalX=0 NormalY=0 NormalZ=1 AngleXU=0 Radius=1.1
    g2: Circle CenterX=5.88896 CenterY=3.40002 CenterZ=0 NormalX=0 NormalY=0 NormalZ=1 AngleXU=0 Radius=1.1
    g3: Circle CenterX=-1.5585e-05 CenterY=-6.79998 CenterZ=0 NormalX=0 NormalY=0 NormalZ=1 AngleXU=0 Radius=1.1
  constraints (8):
    c: Diameter(g0) = 17.8
    c: Coincident(g0,g-1)
    c: Coincident(g1,g-3)
    c: Equal(g1,g-3)
    c: Coincident(g2,g-4)
    c: Equal(g2,g-4)
    c: Coincident(g3,g-5)
    c: Equal(g3,g-5)
FEATURE [PartDesign::Pad] Pad010
  Direction = (1.74533e-07,0,1)
  Length = 63.9
  Length2 = 10
  Profile = -> Sketch018
  ReferenceAxis = -> Sketch018 [N_Axis]
  Reversed = true
  SideType = 0
  Suppressed = false
  Type = 0
  Type2 = 0
FEATURE [PartDesign::SubShapeBinder] Binder003  label="VentHoles_Top"
  BindCopyOnChange = 0
  BindMode = 0
  ClaimChildren = false
  Context = -> Assembly [Body008.Binder003.Edge1]
  Fuse = false
  MakeFace = true
  OffsetFill = false
  OffsetIntersection = false
  OffsetJoinType = 0
  OffsetOpenResult = false
  PartialLoad = false
  Relative = true
  Support = -> [Body002[Pocket008.Edge61,Pocket008.Edge37,Pocket008.Edge42,Pocket008.Edge41,Pocket008.Edge39,Pocket008.Edge27,Pocket008.Edge32,Pocket008.Edge29]]
  _Version = 2
FEATURE [PartDesign::SubShapeBinder] Binder004  label="VentHoles_Bottom"
  BindCopyOnChange = 0
  BindMode = 2
  ClaimChildren = false
  Context = -> Assembly [Body008.Binder004.]
  Fuse = false
  MakeFace = true
  OffsetFill = false
  OffsetIntersection = false
  OffsetJoinType = 0
  OffsetOpenResult = false
  PartialLoad = false
  Placement = pos=(0,0,-63.8) rot=(0,0,1;0rad)
  Relative = true
  _Version = 2
FEATURE [Sketcher::SketchObject] Sketch021
  ArcFitTolerance = 1e-06
  ExternalGeometry = -> [Binder004]
  ExternalTypes = [0]
  FullyConstrained = true
  MakeInternals = false
  MapMode = 5
  Placement = pos=(6.21337e-06,0,35.6) rot=(1,0,0;3.14159rad)
  _ExternalGeoVersion = 0
  sketch-geometry (14):
    g0: Circle CenterX=0 CenterY=0 CenterZ=0 NormalX=0 NormalY=0 NormalZ=1 AngleXU=0 Radius=4.09998
    g1: Circle [constr] CenterX=0 CenterY=0 CenterZ=0 NormalX=0 NormalY=0 NormalZ=1 AngleXU=0 Radius=6.70002
    g2: ArcOfCircle CenterX=-2.29154 CenterY=-6.29596 CenterZ=0 NormalX=0 NormalY=0 NormalZ=1 AngleXU=0 Radius=1.2 StartAngle=1.22173 EndAngle=4.36332
    g3: ArcOfCircle CenterX=2.29153 CenterY=-6.29596 CenterZ=0 NormalX=0 NormalY=0 NormalZ=1 AngleXU=0 Radius=1.2 StartAngle=5.06145 EndAngle=8.20305
    g4: ArcOfCircle CenterX=-4.44985e-06 CenterY=-1.5722e-05 CenterZ=0 NormalX=0 NormalY=0 NormalZ=1 AngleXU=0 Radius=5.5 StartAngle=4.36332 EndAngle=5.06145
    g5: ArcOfCircle CenterX=-4.44985e-06 CenterY=-1.6225e-05 CenterZ=0 NormalX=0 NormalY=0 NormalZ=1 AngleXU=0 Radius=7.9 StartAngle=4.36332 EndAngle=5.06145
    g6: ArcOfCircle CenterX=-4.44985e-06 CenterY=-1.5722e-05 CenterZ=0 NormalX=0 NormalY=0 NormalZ=1 AngleXU=0 Radius=5.5 StartAngle=0.174533 EndAngle=0.872665
    g7: ArcOfCircle CenterX=-4.44985e-06 CenterY=-1.5722e-05 CenterZ=0 NormalX=0 NormalY=0 NormalZ=1 AngleXU=0 Radius=7.9 StartAngle=0.174533 EndAngle=0.872665
    g8: ArcOfCircle CenterX=4.30667 CenterY=5.13248 CenterZ=0 NormalX=0 NormalY=0 NormalZ=1 AngleXU=0 Radius=1.2 StartAngle=0.872665 EndAngle=4.01426
    g9: ArcOfCircle CenterX=6.59821 CenterY=1.16343 CenterZ=0 NormalX=0 NormalY=0 NormalZ=1 AngleXU=0 Radius=1.2 StartAngle=3.31613 EndAngle=6.45771
    g10: ArcOfCircle CenterX=-4.30668 CenterY=5.13248 CenterZ=0 NormalX=0 NormalY=0 NormalZ=1 AngleXU=0 Radius=1.2 StartAngle=5.41052 EndAngle=8.55211
    g11: ArcOfCircle CenterX=-6.59822 CenterY=1.16343 CenterZ=0 NormalX=0 NormalY=0 NormalZ=1 AngleXU=0 Radius=1.2 StartAngle=2.96706 EndAngle=6.10865
    g12: ArcOfCircle CenterX=-5.36395e-06 CenterY=-1.51943e-05 CenterZ=0 NormalX=0 NormalY=0 NormalZ=1 AngleXU=0 Radius=5.5 StartAngle=2.26893 EndAngle=2.96706
    g13: ArcOfCircle CenterX=-4.22077e-06 CenterY=-1.58543e-05 CenterZ=0 NormalX=0 NormalY=0 NormalZ=1 AngleXU=0 Radius=7.9 StartAngle=2.26893 EndAngle=2.96706
  constraints (34):
    c: Coincident(g0,g-1)
    c: Tangent(g0,g-3)
    c: Coincident(g1,g0)
    c: PointOnObject(g-5,g1)
    c: Coincident(g2,g-6)
    c: Coincident(g2,g-8)
    c: Tangent(g2,g-5)
    c: Tangent(g3,g-18) = -1.5708
    c: Coincident(g3,g-18)
    c: Tangent(g4,g-6) = -1.5708
    c: Coincident(g4,g-18)
    c: Coincident(g5,g2)
    c: Coincident(g5,g3)
    c: Tangent(g5,g-8)
    c: Tangent(g6,g-17) = -1.5708
    c: Coincident(g6,g-17)
    c: Tangent(g7,g-15) = -1.5708
    c: Coincident(g7,g-16)
    c: Coincident(g8,g6)
    c: Coincident(g8,g7)
    c: Tangent(g8,g-14)
    c: Coincident(g9,g6)
    c: Coincident(g9,g7)
    c: Tangent(g9,g-16)
    c: Tangent(g10,g-12) = -1.5708
    c: Coincident(g10,g-12)
    c: Tangent(g11,g-11) = -1.5708
    c: Coincident(g11,g-11)
    c: Coincident(g12,g11)
    c: Coincident(g12,g-12)
    c: Tangent(g12,g-9)
    c: Coincident(g13,g10)
    c: Coincident(g13,g11)
    c: Tangent(g13,g-10)
FEATURE [PartDesign::Pocket] Pocket011  label="VentHoles_Bottom_Pocket"
  BaseFeature = -> Pad010
  Direction = (1.74533e-07,1e-16,1)
  Length = 5
  Length2 = 5
  Profile = -> Sketch021
  ReferenceAxis = -> Sketch021 [N_Axis]
  SideType = 0
  Suppressed = false
  Type = 0
  Type2 = 0
FEATURE [Sketcher::SketchObject] Sketch022
  ArcFitTolerance = 1e-06
  AttachmentSupport = -> [Pocket011]
  ExternalGeometry = -> [Binder003]
  ExternalTypes = [0]
  FullyConstrained = true
  MakeInternals = false
  MapMode = 5
  Placement = pos=(1.7366e-05,0,99.5) rot=(0,1.00873,0;0rad)
  _ExternalGeoVersion = 0
  sketch-geometry (13):
    g0: Circle CenterX=0 CenterY=0 CenterZ=0 NormalX=0 NormalY=0 NormalZ=1 AngleXU=0 Radius=4.10002
    g1: ArcOfCircle CenterX=-4.30669 CenterY=-5.13248 CenterZ=0 NormalX=0 NormalY=0 NormalZ=1 AngleXU=0 Radius=1.2 StartAngle=4.01426 EndAngle=7.15585
    g2: ArcOfCircle CenterX=-6.59823 CenterY=-1.16343 CenterZ=0 NormalX=0 NormalY=0 NormalZ=1 AngleXU=0 Radius=1.2 StartAngle=0.174533 EndAngle=3.31613
    g3: ArcOfCircle CenterX=-1.49833e-05 CenterY=1.60694e-05 CenterZ=0 NormalX=0 NormalY=0 NormalZ=1 AngleXU=0 Radius=5.5 StartAngle=3.31613 EndAngle=4.01426
    g4: ArcOfCircle CenterX=-1.60752e-05 CenterY=1.54391e-05 CenterZ=0 NormalX=0 NormalY=0 NormalZ=1 AngleXU=0 Radius=7.9 StartAngle=3.31613 EndAngle=4.01426
    g5: ArcOfCircle CenterX=-1.5585e-05 CenterY=1.5722e-05 CenterZ=0 NormalX=0 NormalY=0 NormalZ=1 AngleXU=0 Radius=5.5 StartAngle=5.41052 EndAngle=6.10865
    g6: ArcOfCircle CenterX=-1.5585e-05 CenterY=1.5722e-05 CenterZ=0 NormalX=0 NormalY=0 NormalZ=1 AngleXU=0 Radius=7.9 StartAngle=5.41052 EndAngle=6.10865
    g7: ArcOfCircle CenterX=4.30666 CenterY=-5.13248 CenterZ=0 NormalX=0 NormalY=0 NormalZ=1 AngleXU=0 Radius=1.2 StartAngle=2.26893 EndAngle=5.41052
    g8: ArcOfCircle CenterX=6.5982 CenterY=-1.16342 CenterZ=0 NormalX=0 NormalY=0 NormalZ=1 AngleXU=0 Radius=1.2 StartAngle=6.10865 EndAngle=9.25025
    g9: ArcOfCircle CenterX=2.29152 CenterY=6.29596 CenterZ=0 NormalX=0 NormalY=0 NormalZ=1 AngleXU=0 Radius=1.2 StartAngle=4.36332 EndAngle=7.50492
    g10: ArcOfCircle CenterX=-2.29155 CenterY=6.29596 CenterZ=0 NormalX=0 NormalY=0 NormalZ=1 AngleXU=0 Radius=1.2 StartAngle=1.91986 EndAngle=5.06145
    g11: ArcOfCircle CenterX=-1.5585e-05 CenterY=1.95751e-05 CenterZ=0 NormalX=0 NormalY=0 NormalZ=1 AngleXU=0 Radius=5.5 StartAngle=1.22173 EndAngle=1.91986
    g12: ArcOfCircle CenterX=-1.5585e-05 CenterY=1.61708e-05 CenterZ=0 NormalX=0 NormalY=0 NormalZ=1 AngleXU=0 Radius=7.9 StartAngle=1.22173 EndAngle=1.91986
  constraints (34):
    c: Coincident(g0,g-1)
    c: Tangent(g0,g-15)
    c: Tangent(g1,g-5) = -1.5708
    c: Coincident(g1,g-5)
    c: Tangent(g2,g-6) = -1.5708
    c: Coincident(g2,g-6)
    c: Coincident(g3,g1)
    c: Coincident(g3,g-6)
    c: Tangent(g3,g-3)
    c: Coincident(g4,g1)
    c: Coincident(g4,g2)
    c: Tangent(g4,g-4)
    c: Coincident(g5,g-13)
    c: Coincident(g5,g-14)
    c: Tangent(g5,g-12)
    c: Coincident(g6,g-13)
    c: Coincident(g6,g-14)
    c: Tangent(g6,g-11)
    c: Coincident(g7,g6)
    c: Coincident(g7,g5)
    c: Tangent(g7,g-14)
    c: Coincident(g8,g6)
    c: Coincident(g8,g5)
    c: Tangent(g8,g-13)
    c: Coincident(g9,g-10)
    c: Tangent(g9,g-9) = -1.5708
    c: Coincident(g10,g-10)
    c: Tangent(g10,g-8) = -1.5708
    c: Coincident(g11,g10)
    c: Coincident(g11,g9)
    c: Tangent(g11,g-7)
    c: Coincident(g12,g10)
    c: Coincident(g12,g9)
    c: Tangent(g12,g-10)
FEATURE [PartDesign::Pocket] Pocket012  label="Ventholes_Top_Pocket"
  BaseFeature = -> Pocket011
  Direction = (-1.74533e-07,0,-1)
  Length = 5
  Length2 = 5
  Profile = -> Sketch022
  ReferenceAxis = -> Sketch022 [N_Axis]
  SideType = 0
  Suppressed = false
  Type = 0
  Type2 = 0
FEATURE [PartDesign::Plane] DatumPlane
  AttachmentOffset = pos=(0,0,0) rot=(1,0,0;1.5708rad)
  AttachmentSupport = -> [Pocket012]
  Length = 65.7798
  MapMode = 5
  Placement = pos=(1.7366e-05,0,99.5) rot=(1.00436,0,0;1.5708rad)
  ResizeMode = 0
  Width = 140.28
FEATURE [Sketcher::SketchObject] Sketch023
  ArcFitTolerance = 1e-06
  AttachmentSupport = -> [DatumPlane]
  ExternalGeometry = -> [Pocket012]
  ExternalTypes = [0]
  FullyConstrained = true
  MakeInternals = false
  MapMode = 5
  Placement = pos=(1.7366e-05,0,99.5) rot=(1,0,0;1.5708rad)
  _ExternalGeoVersion = 0
  sketch-geometry (8):
    g0: GeomPoint X=8.9 Y=-58.9 Z=0
    g1: GeomPoint X=8.9 Y=-5 Z=0
    g2: GeomPoint X=-8.9 Y=-5 Z=0
    g3: GeomPoint X=-8.9 Y=-58.9 Z=0
    g4: LineSegment StartX=-8.9 StartY=-5 StartZ=0 EndX=-8.9 EndY=-58.9 EndZ=0
    g5: LineSegment StartX=-8.9 StartY=-58.9 StartZ=0 EndX=8.9 EndY=-58.9 EndZ=0
    g6: LineSegment StartX=8.9 StartY=-58.9 StartZ=0 EndX=8.9 EndY=-5 EndZ=0
    g7: LineSegment StartX=8.9 StartY=-5 StartZ=0 EndX=-8.9 EndY=-5 EndZ=0
  constraints (18):
    c: PointOnObject(g0,g-3)
    c: PointOnObject(g1,g-3)
    c: DistanceY(g1,g-3) = 5
    c: DistanceY(g-4,g0) = 5
    c: DistanceX(g3,g0) = 17.8
    c: DistanceX(g2,g1) = 17.8
    c: DistanceY(g3,g0) = 0
    c: DistanceY(g2,g1) = 0
    c: Coincident(g4,g5)
    c: Coincident(g5,g6)
    c: Coincident(g6,g7)
    c: Coincident(g7,g4)
    c: Vertical(g4)
    c: Vertical(g6)
    c: Horizontal(g5)
    c: Horizontal(g7)
    c: Coincident(g4,g2)
    c: Coincident(g5,g0)
FEATURE [PartDesign::Pocket] Pocket013  label="CenterCutout"
  BaseFeature = -> Pocket012
  Direction = (0,1,-1e-16)
  Length = 5
  Length2 = 5
  Profile = -> Sketch023
  ReferenceAxis = -> Sketch023 [N_Axis]
  Reversed = true
  SideType = 0
  Suppressed = false
  Type = 1
  Type2 = 0
FEATURE [Sketcher::SketchObject] Sketch024  label="BacksideChannel"
  ArcFitTolerance = 1e-06
  AttachmentOffset = pos=(0,0,-5) rot=(0,0,1;0rad)
  AttachmentSupport = -> [Pocket013]
  ExternalGeometry = -> [Pocket013]
  ExternalTypes = [0]
  FullyConstrained = true
  MakeInternals = false
  MapMode = 5
  Placement = pos=(1.64934e-05,0,94.5) rot=(0,1.00873,0;0rad)
  _ExternalGeoVersion = 0
  sketch-geometry (10):
    g0: LineSegment [constr] StartX=-2.29155 StartY=6.29596 StartZ=0 EndX=-12.2916 EndY=6.29596 EndZ=0
    g1: LineSegment [constr] StartX=-2.29155 StartY=6.29596 StartZ=0 EndX=17.7084 EndY=6.29596 EndZ=0
    g2: ArcOfCircle CenterX=-2.29155 CenterY=6.29596 CenterZ=0 NormalX=0 NormalY=0 NormalZ=1 AngleXU=0 Radius=1.2 StartAngle=3.14159 EndAngle=5.06145
    g3: ArcOfCircle CenterX=2.29152 CenterY=6.29596 CenterZ=0 NormalX=0 NormalY=0 NormalZ=1 AngleXU=0 Radius=1.2 StartAngle=4.36332 EndAngle=6.28319
    g4: GeomPoint X=-6.29054 Y=6.29596 Z=0
    g5: GeomPoint X=6.29054 Y=6.29596 Z=0
    g6: LineSegment StartX=-3.49155 StartY=6.29596 StartZ=0 EndX=-6.29054 EndY=6.29596 EndZ=0
    g7: LineSegment StartX=3.49152 StartY=6.29596 StartZ=0 EndX=6.29054 EndY=6.29596 EndZ=0
    g8: ArcOfCircle CenterX=5.72e-14 CenterY=0 CenterZ=0 NormalX=0 NormalY=0 NormalZ=1 AngleXU=0 Radius=8.9 StartAngle=0.785828 EndAngle=2.35576
    g9: ArcOfCircle CenterX=-1.5585e-05 CenterY=2.11004e-05 CenterZ=0 NormalX=0 NormalY=0 NormalZ=1 AngleXU=0 Radius=5.49999 StartAngle=1.22173 EndAngle=1.91986
  constraints (26):
    c: Distance(g0) = 10
    c: Horizontal(g0)
    c: Coincident(g0,g-5)
    c: Distance(g1) = 20
    c: Coincident(g1,g0)
    c: Horizontal(g1)
    c: Coincident(g2,g0)
    c: Coincident(g2,g-5)
    c: PointOnObject(g2,g0)
    c: Coincident(g3,g-6)
    c: Coincident(g3,g-6)
    c: PointOnObject(g3,g1)
    c: PointOnObject(g4,g-3)
    c: PointOnObject(g5,g-3)
    c: PointOnObject(g5,g1)
    c: PointOnObject(g4,g0)
    c: Coincident(g6,g2)
    c: Coincident(g6,g4)
    c: Coincident(g7,g3)
    c: Coincident(g7,g5)
    c: Coincident(g8,g4)
    c: Coincident(g8,g5)
    c: PointOnObject(g8,g-1)
    c: Coincident(g9,g2)
    c: Coincident(g9,g3)
    c: Tangent(g9,g-4)
FEATURE [PartDesign::Pocket] Pocket014  label="VentilationChannel"
  BaseFeature = -> Pocket013
  Direction = (-1.74533e-07,0,-1)
  Length = 45
  Length2 = 5
  Profile = -> Sketch024
  ReferenceAxis = -> Sketch024 [N_Axis]
  SideType = 0
  Suppressed = false
  Type = 2
  Type2 = 0
FEATURE [Sketcher::SketchObject] Sketch025  label="PCBcutout"
  ArcFitTolerance = 1e-06
  AttachmentSupport = -> [Pocket014]
  ExternalGeometry = -> [Pocket014]
  ExternalTypes = [0]
  FullyConstrained = false
  MakeInternals = false
  MapMode = 5
  Placement = pos=(0,0,0) rot=(1,0,0;1.5708rad)
  _ExternalGeoVersion = 0
  sketch-geometry (23):
    g0: LineSegment [constr] StartX=-7.5 StartY=91.3 StartZ=0 EndX=-7.5 EndY=41.3 EndZ=0
    g1: LineSegment [constr] StartX=-7.5 StartY=41.3 StartZ=0 EndX=7.5 EndY=41.3 EndZ=0
    g2: LineSegment [constr] StartX=7.5 StartY=41.3 StartZ=0 EndX=7.5 EndY=91.3 EndZ=0
    g3: LineSegment [constr] StartX=7.5 StartY=91.3 StartZ=0 EndX=-7.5 EndY=91.3 EndZ=0
    g4: GeomPoint X=-7.7 Y=91.5 Z=0
    g5: GeomPoint X=7.7 Y=41.1 Z=0
    g6: LineSegment [constr] StartX=-7.7 StartY=91.5 StartZ=0 EndX=-7.7 EndY=41.1 EndZ=0
    g7: LineSegment StartX=-7.7 StartY=41.1 StartZ=0 EndX=7.7 EndY=41.1 EndZ=0
    g8: LineSegment [constr] StartX=7.7 StartY=41.1 StartZ=0 EndX=7.7 EndY=91.5 EndZ=0
    g9: LineSegment StartX=7.7 StartY=91.5 StartZ=0 EndX=-7.7 EndY=91.5 EndZ=0
    g10: ArcOfCircle CenterX=-7.7 CenterY=45.8 CenterZ=0 NormalX=0 NormalY=0 NormalZ=1 AngleXU=0 Radius=1.5 StartAngle=4.71239 EndAngle=7.85398
    g11: LineSegment StartX=-7.7 StartY=41.1 StartZ=0 EndX=-7.7 EndY=44.3 EndZ=0
    g12: GeomPoint X=7.7 Y=45.8 Z=0
    g13: ArcOfCircle CenterX=7.7 CenterY=45.8 CenterZ=0 NormalX=0 NormalY=0 NormalZ=1 AngleXU=0 Radius=1.5 StartAngle=1.5708 EndAngle=4.71239
    g14: LineSegment StartX=7.7 StartY=44.3 StartZ=0 EndX=7.7 EndY=41.1 EndZ=0
    g15: GeomPoint X=-7.7 Y=85.8 Z=0
    g16: ArcOfCircle CenterX=-7.7 CenterY=85.8 CenterZ=0 NormalX=0 NormalY=0 NormalZ=1 AngleXU=0 Radius=1.5 StartAngle=4.71239 EndAngle=7.85398
    g17: LineSegment StartX=-7.7 StartY=84.3 StartZ=0 EndX=-7.7 EndY=47.3 EndZ=0
    g18: LineSegment StartX=-7.7 StartY=87.3 StartZ=0 EndX=-7.7 EndY=91.5 EndZ=0
    g19: GeomPoint X=7.7 Y=85.8 Z=0
    g20: ArcOfCircle CenterX=7.7 CenterY=85.8 CenterZ=0 NormalX=0 NormalY=0 NormalZ=1 AngleXU=0 Radius=1.5 StartAngle=1.5708 EndAngle=4.71239
    g21: LineSegment StartX=7.7 StartY=87.3 StartZ=0 EndX=7.7 EndY=91.5 EndZ=0
    g22: LineSegment StartX=7.7 StartY=84.3 StartZ=0 EndX=7.7 EndY=47.3 EndZ=0
  constraints (60):
    c: Coincident(g0,g1)
    c: Coincident(g1,g2)
    c: Coincident(g2,g3)
    c: Coincident(g3,g0)
    c: Vertical(g0)
    c: Vertical(g2)
    c: Horizontal(g1)
    c: Horizontal(g3)
    c: DistanceX(g0,g2) = 15
    c: DistanceY(g0,g0) = 50
    c: DistanceX(g0,g-1) = 7.5
    c: DistanceX(g1,g5) = 0.2
    c: DistanceX(g4,g0) = 0.2
    c: DistanceY(g0,g4) = 0.2
    c: DistanceY(g5,g1) = 0.2
    c: Coincident(g6,g7)
    c: Coincident(g7,g8)
    c: Coincident(g8,g9)
    c: Coincident(g9,g6)
    c: Vertical(g6)
    c: Vertical(g8)
    c: Horizontal(g7)
    c: Horizontal(g9)
    c: Coincident(g6,g4)
    c: Coincident(g7,g5)
    c: PointOnObject(g10,g6)
    c: PointOnObject(g10,g6)
    c: PointOnObject(g10,g6)
    c: Radius(g10) = 1.5
    c: DistanceY(g0,g10) = 4.5
    c: DistanceY(g11,g0) = 0.2
    c: DistanceX(g11,g0) = 0.2
    c: PointOnObject(g12,g8)
    c: DistanceY(g10,g12) = 0
    c: Coincident(g13,g12)
    c: PointOnObject(g13,g8)
    c: PointOnObject(g13,g8)
    c: Radius(g13) = 1.5
    c: Coincident(g14,g13)
    c: Coincident(g14,g5)
    c: Coincident(g11,g10)
    c: DistanceY(g15,g0) = 5.5
    c: Coincident(g16,g15)
    c: Radius(g16) = 1.5
    c: Coincident(g17,g16)
    c: Coincident(g17,g10)
    c: Vertical(g17)
    c: Coincident(g18,g16)
    c: Coincident(g18,g4)
    c: Vertical(g18)
    c: DistanceY(g15,g19) = 0
    c: Coincident(g20,g19)
    c: Radius(g20) = 1.5
    c: Coincident(g21,g20)
    c: Coincident(g21,g8)
    c: Vertical(g21)
    c: Coincident(g22,g20)
    c: Coincident(g22,g13)
    c: Vertical(g22)
    c: DistanceY(g-6,g0) = 0.7
FEATURE [Sketcher::SketchObject] Sketch026  label="BMEcutout"
  ArcFitTolerance = 1e-06
  AttachmentSupport = -> [Pocket014]
  ExternalGeometry = -> [Pocket014]
  ExternalTypes = [0]
  FullyConstrained = true
  MakeInternals = false
  MapMode = 5
  Placement = pos=(7.08603e-06,0,40.6) rot=(1,0,0;3.14159rad)
  _ExternalGeoVersion = 0
  sketch-geometry (2):
    g0: ArcOfCircle CenterX=3.3e-15 CenterY=0 CenterZ=0 NormalX=0 NormalY=0 NormalZ=1 AngleXU=0 Radius=4.09998 StartAngle=3.14159 EndAngle=6.28319
    g1: LineSegment StartX=-4.09998 StartY=5e-16 StartZ=0 EndX=4.09998 EndY=-1e-15 EndZ=0
  constraints (4):
    c: Tangent(g0,g-3) = -1.5708
    c: Coincident(g0,g-3)
    c: Coincident(g1,g0)
    c: Coincident(g1,g0)
FEATURE [PartDesign::Pocket] Pocket015  label="BMEcutoutPocket"
  BaseFeature = -> Pocket014
  Direction = (1.74533e-07,0,1)
  Length = 7.5
  Length2 = 5
  Profile = -> Sketch026
  ReferenceAxis = -> Sketch026 [N_Axis]
  SideType = 0
  Suppressed = false
  Type = 0
  Type2 = 0
FEATURE [PartDesign::Pocket] Pocket016  label="PCBcutoutPocket"
  BaseFeature = -> Pocket015
  Direction = (0,1,-2e-16)
  Length = 0.7
  Length2 = 5
  Profile = -> Sketch025
  ReferenceAxis = -> Sketch025 [N_Axis]
  SideType = 0
  Suppressed = false
  Type = 0
  Type2 = 0
FEATURE [PartDesign::Body] Body008  label="Center"
  AllowCompound = false
  Group = -> [Binder002,Sketch018,Pad010,Binder003,Binder004,Sketch021,Pocket011,Sketch022,Pocket012,DatumPlane,Sketch023,Pocket013,Sketch024,Pocket014,Sketch025,Sketch026,Pocket015,Pocket016]
  Origin = -> Origin009
  Placement = pos=(0,-5.72205e-06,36.0001) rot=(0,0,1;0rad)
  Tip = -> Pocket016
FEATURE [PartDesign::Plane] DatumPlane001
  AttachmentOffset = pos=(0,-80,-2) rot=(0,0,1;0rad)
  AttachmentSupport = -> [Pocket016]
  Length = 69.3866
  MapMode = 45
  Placement = pos=(2.57523e-05,-0.0934557,147.55) rot=(-1,0,0;1.5708rad)
  ResizeMode = 0
  Width = 207.307
FEATURE [Sketcher::SketchObject] Sketch027
  ArcFitTolerance = 1e-06
  AttachmentSupport = -> [DatumPlane001]
  ExternalTypes = [0]
  FullyConstrained = true
  MakeInternals = false
  MapMode = 5
  Placement = pos=(2.57523e-05,-0.0934557,147.55) rot=(-1,0,0;1.5708rad)
  _ExternalGeoVersion = 0
  sketch-geometry (23):
    g0: LineSegment StartX=-5.2 StartY=7.35 StartZ=0 EndX=-3.2 EndY=7.35 EndZ=0
    g1: LineSegment StartX=-3.2 StartY=9.85 StartZ=0 EndX=-3.2 EndY=7.35 EndZ=0
    g2: LineSegment StartX=-3.2 StartY=9.85 StartZ=0 EndX=-4 EndY=9.85 EndZ=0
    g3: LineSegment StartX=-4 StartY=9.85 StartZ=0 EndX=-4 EndY=11.63 EndZ=0
    g4: LineSegment StartX=-2 StartY=11.63 StartZ=0 EndX=-2 EndY=-15.37 EndZ=0
    g5: LineSegment StartX=-4 StartY=11.63 StartZ=0 EndX=-2 EndY=11.63 EndZ=0
    g6: LineSegment StartX=-5.2 StartY=7.35 StartZ=0 EndX=-5.2 EndY=4.85 EndZ=0
    g7: LineSegment StartX=-2.7 StartY=0.85 StartZ=0 EndX=-3.5 EndY=0.85 EndZ=0
    g8: LineSegment StartX=-2.7 StartY=2.85 StartZ=0 EndX=-2.7 EndY=0.85 EndZ=0
    g9: LineSegment StartX=-3.5 StartY=0.85 StartZ=0 EndX=-3.5 EndY=-3.15 EndZ=0
    g10: LineSegment StartX=-2.7 StartY=-3.37 StartZ=0 EndX=-2.7 EndY=-5.37 EndZ=0
    g11: LineSegment StartX=-2.7 StartY=-5.37 StartZ=0 EndX=-3.5 EndY=-5.37 EndZ=0
    g12: LineSegment StartX=-3.5 StartY=-9.37 StartZ=0 EndX=-2.7 EndY=-9.37 EndZ=0
    g13: LineSegment StartX=-2.7 StartY=-9.37 StartZ=0 EndX=-2.7 EndY=-11.37 EndZ=0
    g14: LineSegment StartX=-2.7 StartY=-11.37 StartZ=0 EndX=-3.5 EndY=-11.37 EndZ=0
    g15: LineSegment StartX=-3.5 StartY=-11.37 StartZ=0 EndX=-3.5 EndY=-15.37 EndZ=0
    g16: LineSegment StartX=-3.5 StartY=-15.37 StartZ=0 EndX=-2 EndY=-15.37 EndZ=0
    g17: LineSegment StartX=-3.5 StartY=2.85 StartZ=0 EndX=-2.7 EndY=2.85 EndZ=0
    g18: LineSegment StartX=-5.2 StartY=4.85 StartZ=0 EndX=-4.35 EndY=4.85 EndZ=0
    g19: ArcOfCircle CenterX=-4.66305 CenterY=3.72266 CenterZ=0 NormalX=0 NormalY=0 NormalZ=1 AngleXU=0 Radius=1.17 StartAngle=0.109055 EndAngle=1.29993
    g20: LineSegment StartX=-3.5 StartY=3.85 StartZ=0 EndX=-3.5 EndY=2.85 EndZ=0
    g21: LineSegment StartX=-3.5 StartY=-5.37 StartZ=0 EndX=-3.5 EndY=-9.37 EndZ=0
    g22: LineSegment StartX=-3.5 StartY=-3.15 StartZ=0 EndX=-2.7 EndY=-3.37 EndZ=0
  constraints (70):
    c: Coincident(g18,g19)
    c: DistanceX(g16,g-1) = 2
    c: Coincident(g4,g16)
    c: DistanceX(g16,g16) = 1.5
    c: DistanceY(g16,g4) = 0
    c: Coincident(g15,g16)
    c: DistanceX(g14,g14) = 0.8
    c: DistanceY(g15,g15) = 4
    c: DistanceY(g14,g14) = 0
    c: DistanceX(g15,g15) = 0
    c: Coincident(g14,g15)
    c: Coincident(g13,g14)
    c: DistanceY(g13,g13) = 2
    c: DistanceX(g12,g13) = 0
    c: Coincident(g12,g13)
    c: DistanceX(g12,g12) = 0.8
    c: DistanceY(g12,g12) = 0
    c: DistanceY(g4,g4) = 27
    c: Coincident(g21,g11)
    c: Coincident(g21,g12)
    c: Vertical(g21)
    c: DistanceY(g21,g21) = 4
    c: DistanceY(g11,g10) = 0
    c: DistanceX(g11,g10) = 0.8
    c: Coincident(g11,g10)
    c: DistanceY(g10,g10) = 2
    c: DistanceX(g10,g10) = 0
    c: DistanceY(g4,g-1) = 15.37
    c: DistanceX(g4,g4) = 0
    c: DistanceY(g5,g5) = 0
    c: Coincident(g5,g4)
    c: DistanceX(g5,g5) = 2
    c: Coincident(g3,g5)
    c: DistanceY(g3,g3) = 1.78
    c: DistanceX(g3,g4) = 2
    c: Coincident(g2,g3)
    c: DistanceX(g2,g2) = 0.8
    c: DistanceY(g2,g2) = 0
    c: Coincident(g1,g2)
    c: DistanceY(g1,g1) = 2.5
    c: DistanceX(g1,g1) = 0
    c: Coincident(g0,g1)
    c: DistanceX(g0,g0) = 2
    c: DistanceY(g0,g0) = 0
    c: Coincident(g6,g0)
    c: DistanceY(g6,g6) = 2.5
    c: Coincident(g6,g18)
    c: DistanceX(g6,g0) = 0
    c: DistanceX(g18,g18) = 0.85
    c: DistanceY(g6,g18) = 0
    c: DistanceX(g19,g0) = 0.3
    c: DistanceY(g19,g18) = 1
    c: Radius(g19) = 1.17
    c: Coincident(g20,g19)
    c: DistanceY(g20,g20) = 1
    c: DistanceX(g19,g17) = 0
    c: Coincident(g17,g20)
    c: DistanceY(g8,g8) = 2
    c: DistanceY(g17,g8) = 0
    c: DistanceX(g17,g8) = 0.8
    c: Coincident(g17,g8)
    c: DistanceX(g8,g8) = 0
    c: Coincident(g7,g8)
    c: DistanceX(g7,g7) = 0.8
    c: DistanceY(g7,g7) = 0
    c: Coincident(g9,g7)
    c: DistanceY(g9,g9) = 4
    c: DistanceX(g7,g9) = 0
    c: Coincident(g22,g9)
    c: Coincident(g22,g10)
FEATURE [PartDesign::Revolution] Revolution
  Angle = 360
  Angle2 = 60
  Axis = (-1.74533e-07,3e-16,-1)
  Base = (2.57523e-05,-0.0934557,147.55)
  FuseOrder = 1
  Placement = pos=(2.57523e-05,-0.0934557,147.55) rot=(-1,0,0;1.5708rad)
  Profile = -> Sketch027
  ReferenceAxis = -> Sketch027 [V_Axis]
  Suppressed = false
  Type = 0
FEATURE [PartDesign::Body] Body009  label="CableProtector"
  AllowCompound = false
  Group = -> [DatumPlane001,Sketch027,Revolution]
  Origin = -> Origin010
  Placement = pos=(0,0,-1.4) rot=(0,0,1;0rad)
  Tip = -> Revolution
FEATURE [App::FeaturePython] Move  # WARN: FeaturePython — macro-defined, semantics opaque (R4)
  MoveType = 0
  MovementTransform = pos=(0,-1e-05,99) rot=(0,0,1;0rad)
  References = -> Assembly [Body009.]
FEATURE [App::FeaturePython] Move001  # WARN: FeaturePython — macro-defined, semantics opaque (R4)
  MoveType = 0
  MovementTransform = pos=(3e-05,1e-05,84) rot=(0,0,1;0rad)
  References = -> Assembly [Body002.]
FEATURE [App::FeaturePython] Move002  # WARN: FeaturePython — macro-defined, semantics opaque (R4)
  MoveType = 0
  MovementTransform = pos=(0,-1e-05,63) rot=(0,0,1;0rad)
  References = -> Assembly [Body006.]
FEATURE [App::FeaturePython] Move003  # WARN: FeaturePython — macro-defined, semantics opaque (R4)
  MoveType = 0
  MovementTransform = pos=(0,-1e-05,55.0001) rot=(0,0,1;0rad)
  References = -> Assembly [Body004.]
FEATURE [App::FeaturePython] Move004  # WARN: FeaturePython — macro-defined, semantics opaque (R4)
  MoveType = 0
  MovementTransform = pos=(0,0,38.0001) rot=(0,0,1;0rad)
  References = -> Assembly [Body008.]
FEATURE [App::FeaturePython] Move005  # WARN: FeaturePython — macro-defined, semantics opaque (R4)
  MoveType = 0
  MovementTransform = pos=(0,1e-05,-57.0001) rot=(0,0,1;0rad)
  References = -> Assembly [Body.]
FEATURE [App::FeaturePython] Move006  # WARN: FeaturePython — macro-defined, semantics opaque (R4)
  MoveType = 0
  MovementTransform = pos=(0,1e-05,-42.0001) rot=(0,0,1;0rad)
  References = -> Assembly [Body007.]
FEATURE [App::FeaturePython] Move007  # WARN: FeaturePython — macro-defined, semantics opaque (R4)
  MoveType = 0
  MovementTransform = pos=(0,0,-37.0001) rot=(0,0,1;0rad)
  References = -> Assembly [Body005.]
FEATURE [App::FeaturePython] Move008  # WARN: FeaturePython — macro-defined, semantics opaque (R4)
  MoveType = 0
  MovementTransform = pos=(0,0,-27.0001) rot=(0,0,1;0rad)
  References = -> Assembly [Body001.]
FEATURE [Sketcher::SketchObject] Sketch028
  ArcFitTolerance = 1e-06
  AttachmentSupport = -> [XZ_Plane011]
  ExternalTypes = [0]
  FullyConstrained = true
  MakeInternals = false
  MapMode = 5
  Placement = pos=(0,0,0) rot=(1,0,0;1.5708rad)
  _ExternalGeoVersion = 0
  sketch-geometry (6):
    g0: LineSegment StartX=0 StartY=0 StartZ=0 EndX=0 EndY=7 EndZ=0
    g1: LineSegment StartX=0 StartY=7 StartZ=0 EndX=1 EndY=7 EndZ=0
    g2: LineSegment StartX=1 StartY=7 StartZ=0 EndX=1 EndY=1.5 EndZ=0
    g3: LineSegment StartX=1 StartY=1.5 StartZ=0 EndX=1.9 EndY=1.5 EndZ=0
    g4: LineSegment StartX=1.9 StartY=1.5 StartZ=0 EndX=1.9 EndY=1 EndZ=0
    g5: ArcOfCircle CenterX=0 CenterY=2.305 CenterZ=0 NormalX=0 NormalY=0 NormalZ=1 AngleXU=0 Radius=2.305 StartAngle=4.71239 EndAngle=5.68134
  constraints (18):
    c: Distance(g0) = 7
    c: Coincident(g0,g-1)
    c: PointOnObject(g0,g-2)
    c: Distance(g1) = 1
    c: Coincident(g1,g0)
    c: Horizontal(g1)
    c: Distance(g2) = 5.5
    c: Coincident(g2,g1)
    c: Vertical(g2)
    c: Distance(g3) = 0.9
    c: Coincident(g3,g2)
    c: Horizontal(g3)
    c: Distance(g4) = 0.5
    c: Coincident(g4,g3)
    c: Vertical(g4)
    c: Coincident(g5,g4)
    c: Coincident(g5,g0)
    c: PointOnObject(g5,g0)
FEATURE [PartDesign::Revolution] Revolution001
  Angle = 360
  Angle2 = 60
  Axis = (0,2e-16,1)
  Base = (0,0,0)
  FuseOrder = 1
  Placement = pos=(0,0,0) rot=(1,0,0;1.5708rad)
  Profile = -> Sketch028
  ReferenceAxis = -> Sketch028 [V_Axis]
  Reversed = true
  Suppressed = false
  Type = 0
FEATURE [Sketcher::SketchObject] Sketch029
  ArcFitTolerance = 1e-06
  AttachmentSupport = -> [Revolution001]
  ExternalTypes = [0]
  FullyConstrained = true
  MakeInternals = false
  MapMode = 5
  Placement = pos=(0,7e-16,1.5) rot=(0,0,1;3.14159rad)
  _ExternalGeoVersion = 0
  sketch-geometry (6):
    g0: LineSegment StartX=-0.5 StartY=0.866025 StartZ=0 EndX=0.5 EndY=0.866025 EndZ=0
    g1: LineSegment StartX=0.5 StartY=0.866025 StartZ=0 EndX=1 EndY=0 EndZ=0
    g2: LineSegment StartX=0.5 StartY=-0.866025 StartZ=0 EndX=-0.5 EndY=-0.866025 EndZ=0
    g3: LineSegment StartX=-0.5 StartY=-0.866025 StartZ=0 EndX=-1 EndY=0 EndZ=0
    g4: LineSegment StartX=-1 StartY=0 StartZ=0 EndX=-0.5 EndY=0.866025 EndZ=0
    g5: LineSegment StartX=0.5 StartY=-0.866025 StartZ=0 EndX=1 EndY=0 EndZ=0
  constraints (18):
    c: Horizontal(g0)
    c: Coincident(g1,g0)
    c: Horizontal(g2)
    c: Coincident(g3,g2)
    c: Coincident(g4,g3)
    c: Coincident(g4,g0)
    c: DistanceX(g0,g0) = 1
    c: DistanceX(g2,g0) = 0
    c: PointOnObject(g3,g-1)
    c: PointOnObject(g1,g-1)
    c: DistanceX(g2,g2) = 1
    c: Coincident(g5,g2)
    c: Coincident(g5,g1)
    c: Distance(g5,g5) = 1
    c: Distance(g1,g1) = 1
    c: Distance(g4,g4) = 1
    c: DistanceX(g0,g-1) = 0.5
    c: Angle(g4,g0) = 2.0944
FEATURE [PartDesign::Pocket] Pocket017
  BaseFeature = -> Revolution001
  Direction = (0,0,-1)
  Length = 5
  Length2 = 5
  Placement = pos=(0,0,0) rot=(1,0,0;1.5708rad)
  Profile = -> Sketch029
  ReferenceAxis = -> Sketch029 [N_Axis]
  SideType = 0
  Suppressed = false
  Type = 1
  Type2 = 0
FEATURE [PartDesign::Body] Body010  label="HexBolt"
  AllowCompound = false
  Group = -> [Sketch028,Revolution001,Sketch029,Pocket017]
  Origin = -> Origin011
  Tip = -> Pocket017
FEATURE [App::Link] HexBolt  label="HexBolt_Bottom_1"
  LinkPlacement = pos=(0,-6.8,68) rot=(0,0,1;0rad)
  LinkedObject = -> Body010
  Placement = pos=(0,-6.8,68) rot=(0,0,1;0rad)
FEATURE [App::Link] HexBolt001  label="HexBolt_Bottom_2"
  LinkPlacement = pos=(-5.91,3.4,68.21) rot=(0,0,1;0rad)
  LinkedObject = -> Body010
  Placement = pos=(-5.91,3.4,68.21) rot=(0,0,1;0rad)
FEATURE [App::Link] HexBolt002  label="HexBolt_Bottom_3"
  LinkPlacement = pos=(5.85,3.4,68) rot=(0,0,1;0rad)
  LinkedObject = -> Body010
  Placement = pos=(5.85,3.4,68) rot=(0,0,1;0rad)
FEATURE [App::FeaturePython] Move009  # WARN: FeaturePython — macro-defined, semantics opaque (R4)
  MoveType = 0
  MovementTransform = pos=(0,1e-05,-73) rot=(0,0,1;0rad)
  References = -> Assembly [HexBolt.,HexBolt001.,HexBolt002.]
FEATURE [App::Link] HexBolt003  label="HexBolt_Top_1"
  LinkPlacement = pos=(1.18532e-05,-6.99999,139.169) rot=(0,1,0;3.14159rad)
  LinkedObject = -> Body010
  Placement = pos=(1.18532e-05,-6.99999,139.169) rot=(0,1,0;3.14159rad)
FEATURE [App::Link] HexBolt004  label="HexBolt_Top_2"
  LinkPlacement = pos=(-5.88,3.5,138.99) rot=(0,1,0;3.14159rad)
  LinkedObject = -> Body010
  Placement = pos=(-5.88,3.5,138.99) rot=(0,1,0;3.14159rad)
FEATURE [App::Link] HexBolt005  label="HexBolt_Top_3"
  LinkPlacement = pos=(6,3.5,139.17) rot=(0,1,0;3.14159rad)
  LinkedObject = -> Body010
  Placement = pos=(6,3.5,139.17) rot=(0,1,0;3.14159rad)
FEATURE [App::FeaturePython] Move010  # WARN: FeaturePython — macro-defined, semantics opaque (R4)
  MoveType = 0
  MovementTransform = pos=(-1e-05,2e-05,131) rot=(0,1.00436,0;0rad)
  References = -> Assembly [HexBolt004.,HexBolt005.,HexBolt003.]
FEATURE [App::FeaturePython] Exploded_View  # WARN: FeaturePython — macro-defined, semantics opaque (R4)
  Group = -> [Move,Move001,Move002,Move003,Move004,Move005,Move006,Move007,Move008,Move009,Move010]
FEATURE [Assembly::ViewGroup] Exploded_Views
  Group = -> [Exploded_View]
FEATURE [App::Point] Origin012  label="Origin"
  Role = Origin
FEATURE [App::Point] Origin013  label="Origin"
  Role = Origin
FEATURE [App::Point] Origin014  label="Origin"
  Role = Origin
FEATURE [App::Point] Origin015  label="Origin"
  Role = Origin
FEATURE [App::Point] Origin016  label="Origin"
  Role = Origin
FEATURE [App::Point] Origin017  label="Origin"
  Role = Origin
FEATURE [App::Point] Origin018  label="Origin"
  Role = Origin
FEATURE [App::Point] Origin019  label="Origin"
  Role = Origin
FEATURE [App::Point] Origin020  label="Origin"
  Role = Origin
FEATURE [App::Point] Origin021  label="Origin"
  Role = Origin
FEATURE [App::Point] Origin022  label="Origin"
  Role = Origin
FEATURE [PartDesign::SubShapeBinder] Binder006
  BindCopyOnChange = 0
  BindMode = 0
  ClaimChildren = false
  Context = -> Assembly [Body012.Binder006.]
  Fuse = false
  MakeFace = true
  OffsetFill = false
  OffsetIntersection = false
  OffsetJoinType = 0
  OffsetOpenResult = false
  PartialLoad = false
  Relative = true
  Support = -> [Body011[Pocket023.Edge61,Pocket023.Edge58,Pocket023.Edge62,Pocket023.Edge60,Pocket023.Edge59]]
  _Version = 2
FEATURE [PartDesign::SubShapeBinder] Binder007
  BindCopyOnChange = 0
  BindMode = 0
  ClaimChildren = false
  Context = -> Assembly [Body012.Binder007.]
  Fuse = false
  MakeFace = true
  OffsetFill = false
  OffsetIntersection = false
  OffsetJoinType = 0
  OffsetOpenResult = false
  PartialLoad = false
  Refine = true
  Relative = true
  Support = -> [Body011[Pocket023.Edge51,Pocket023.Edge56,Pocket023.Edge55,Pocket023.Edge53,Pocket023.Edge42,Pocket023.Edge37,Pocket023.Edge39,Pocket023.Edge41]]
  _Version = 2
FEATURE [App::Point] Origin025
  Role = Origin
FEATURE [App::Point] Origin026
  Role = Origin
FEATURE [PartDesign::Pad] Pad013
  Direction = (1.74533e-07,0,1)
  Length = 0.25
  Length2 = 10
  Profile = -> Binder006
  SideType = 0
  Suppressed = false
  Type = 0
  Type2 = 0
FEATURE [PartDesign::Pocket] Pocket024
  BaseFeature = -> Pad013
  Direction = (-1.74533e-07,0,-1)
  Length = 5
  Length2 = 5
  Profile = -> Binder007
  Reversed = true
  SideType = 0
  Suppressed = false
  Type = 1
  Type2 = 0
FEATURE [PartDesign::Body] Body012  label="MeshMask_Top"
  AllowCompound = false
  Group = -> [Binder006,Pad013,Binder007,Pocket024]
  Origin = -> Origin024
  Placement = pos=(0,0,53.8) rot=(0,0,1;0rad)
  Tip = -> Pocket024
FEATURE [Sketcher::SketchObject] Sketch030  label="22mmCircle002"
  ArcFitTolerance = 1e-06
  AttachmentSupport = -> [XY_Plane012]
  ExternalTypes = [0]
  FullyConstrained = true
  MakeInternals = false
  MapMode = 5
  _ExternalGeoVersion = 0
  sketch-geometry (1):
    g0: Circle CenterX=0 CenterY=0 CenterZ=0 NormalX=0 NormalY=0 NormalZ=1 AngleXU=0 Radius=11
  constraints (2):
    c: Diameter(g0) = 22
    c: Coincident(g0,g-1)
FEATURE [PartDesign::Pad] Pad011
  Direction = (0,0,1)
  Length = 8.5
  Length2 = 10
  Profile = -> Sketch030
  ReferenceAxis = -> Sketch030 [N_Axis]
  SideType = 0
  Suppressed = false
  Type = 0
  Type2 = 0
FEATURE [Sketcher::SketchObject] Sketch031
  ArcFitTolerance = 1e-06
  AttachmentSupport = -> [Pad011]
  ExternalTypes = [0]
  FullyConstrained = true
  MakeInternals = false
  MapMode = 5
  Placement = pos=(0,0,8.5) rot=(0,0,1;0rad)
  _ExternalGeoVersion = 0
  sketch-geometry (1):
    g0: Circle CenterX=0 CenterY=0 CenterZ=0 NormalX=0 NormalY=0 NormalZ=1 AngleXU=0 Radius=9.85
  constraints (2):
    c: Diameter(g0) = 19.7
    c: Coincident(g0,g-1)
FEATURE [PartDesign::Pad] Pad012
  BaseFeature = -> Pad011
  Direction = (0,0,1)
  Length = 2.5
  Length2 = 10
  Profile = -> Sketch031
  ReferenceAxis = -> Sketch031 [N_Axis]
  SideType = 0
  Suppressed = false
  Type = 0
  Type2 = 0
FEATURE [Sketcher::SketchObject] Sketch032
  ArcFitTolerance = 1e-06
  AttachmentSupport = -> [Pad012]
  ExternalTypes = [0]
  FullyConstrained = true
  MakeInternals = false
  MapMode = 5
  Placement = pos=(0,0,11) rot=(0,0,1;0rad)
  _ExternalGeoVersion = 0
  sketch-geometry (1):
    g0: Circle CenterX=0 CenterY=0 CenterZ=0 NormalX=0 NormalY=0 NormalZ=1 AngleXU=0 Radius=9
  constraints (2):
    c: Diameter(g0) = 18
    c: Coincident(g0,g-1)
FEATURE [PartDesign::Pocket] Pocket019
  BaseFeature = -> Pad012
  Direction = (0,0,-1)
  Length = 7.5
  Length2 = 5
  Profile = -> Sketch032
  ReferenceAxis = -> Sketch032 [N_Axis]
  SideType = 0
  Suppressed = false
  Type = 0
  Type2 = 0
FEATURE [Sketcher::SketchObject] Sketch033  label="BoltHoles_outer002"
  ArcFitTolerance = 1e-06
  AttachmentSupport = -> [Pocket019]
  ExternalGeometry = -> [Pocket019]
  ExternalTypes = [0]
  FullyConstrained = true
  MakeInternals = false
  MapMode = 5
  Placement = pos=(0,0,0) rot=(1,0,0;3.14159rad)
  _ExternalGeoVersion = 0
  sketch-geometry (5):
    g0: Circle CenterX=0 CenterY=6.8 CenterZ=0 NormalX=0 NormalY=0 NormalZ=1 AngleXU=0 Radius=1.95
    g1: Circle CenterX=-5.88897 CenterY=-3.4 CenterZ=0 NormalX=0 NormalY=0 NormalZ=1 AngleXU=0 Radius=1.95
    g2: Circle CenterX=5.88897 CenterY=-3.4 CenterZ=0 NormalX=0 NormalY=0 NormalZ=1 AngleXU=0 Radius=1.95
    g3: LineSegment [constr] StartX=0 StartY=0 StartZ=0 EndX=5.88897 EndY=-3.4 EndZ=0
    g4: LineSegment [constr] StartX=-5.88897 StartY=-3.4 StartZ=0 EndX=0 EndY=0 EndZ=0
  constraints (13):
    c: Diameter(g0) = 3.9
    c: PointOnObject(g0,g-2)
    c: Diameter(g1) = 3.9
    c: Diameter(g2) = 3.9
    c: Distance(g-1,g0) = 6.8
    c: Distance(g-1,g1) = 6.8
    c: Distance(g-1,g2) = 6.8
    c: Coincident(g3,g-1)
    c: Coincident(g3,g2)
    c: Angle(g3,g-2) = 2.0944
    c: Coincident(g4,g1)
    c: Coincident(g4,g3)
    c: Angle(g-2,g4) = 2.0944
FEATURE [PartDesign::Pocket] Pocket020
  BaseFeature = -> Pocket019
  Direction = (0,0,1)
  Length = 1.5
  Length2 = 5
  Profile = -> Sketch033
  ReferenceAxis = -> Sketch033 [N_Axis]
  SideType = 0
  Suppressed = false
  Type = 0
  Type2 = 0
FEATURE [PartDesign::Fillet] Fillet010
  Base = -> Pocket020 [Edge2]
  BaseFeature = -> Pocket020
  Radius = 1.2
  SupportTransform = false
  Suppressed = false
  UseAllEdges = false
FEATURE [Sketcher::SketchObject] Sketch034  label="BoltHoles_inner002"
  ArcFitTolerance = 1e-06
  AttachmentSupport = -> [Fillet010]
  ExternalGeometry = -> [Fillet010]
  ExternalTypes = [0]
  FullyConstrained = true
  MakeInternals = false
  MapMode = 5
  Placement = pos=(0,0,1.5) rot=(1,0,0;3.14159rad)
  _ExternalGeoVersion = 0
  sketch-geometry (3):
    g0: Circle CenterX=-5.88897 CenterY=-3.4 CenterZ=0 NormalX=0 NormalY=0 NormalZ=1 AngleXU=0 Radius=1.1
    g1: Circle CenterX=0 CenterY=6.8 CenterZ=0 NormalX=0 NormalY=0 NormalZ=1 AngleXU=0 Radius=1.1
    g2: Circle CenterX=5.88897 CenterY=-3.4 CenterZ=0 NormalX=0 NormalY=0 NormalZ=1 AngleXU=0 Radius=1.1
  constraints (6):
    c: Diameter(g0) = 2.2
    c: Coincident(g0,g-4)
    c: Diameter(g1) = 2.2
    c: Coincident(g1,g-3)
    c: Diameter(g2) = 2.2
    c: Coincident(g2,g-5)
FEATURE [PartDesign::Pocket] Pocket021
  BaseFeature = -> Fillet010
  Direction = (0,0,1)
  Length = 2
  Length2 = 5
  Profile = -> Sketch034
  ReferenceAxis = -> Sketch034 [N_Axis]
  SideType = 0
  Suppressed = false
  Type = 0
  Type2 = 0
FEATURE [Sketcher::SketchObject] Sketch035  label="VentHoles002"
  ArcFitTolerance = 1e-06
  AttachmentSupport = -> [Pocket021]
  ExternalGeometry = -> [Pocket021]
  ExternalTypes = [0]
  FullyConstrained = true
  MakeInternals = false
  MapMode = 5
  Placement = pos=(0,0,0) rot=(1,0,0;3.14159rad)
  _ExternalGeoVersion = 0
  sketch-geometry (33):
    g0: Circle [constr] CenterX=0 CenterY=0 CenterZ=0 NormalX=0 NormalY=0 NormalZ=1 AngleXU=0 Radius=7.9
    g1: Circle [constr] CenterX=0 CenterY=0 CenterZ=0 NormalX=0 NormalY=0 NormalZ=1 AngleXU=0 Radius=5.5
    g2: Circle CenterX=0 CenterY=0 CenterZ=0 NormalX=0 NormalY=0 NormalZ=1 AngleXU=0 Radius=3.3
    g3: LineSegment [constr] StartX=0 StartY=0 StartZ=0 EndX=-6.29932 EndY=7.50724 EndZ=0
    g4: LineSegment [constr] StartX=0 StartY=0 StartZ=0 EndX=-9.65112 EndY=1.70175 EndZ=0
    g5: GeomPoint X=-5.07802 Y=6.05175 Z=0
    g6: GeomPoint X=-3.53533 Y=4.21324 Z=0
    g7: ArcOfCircle CenterX=-4.30668 CenterY=5.1325 CenterZ=0 NormalX=0 NormalY=0 NormalZ=1 AngleXU=0 Radius=1.2 StartAngle=5.41052 EndAngle=8.55211
    g8: GeomPoint X=-7.77998 Y=1.37182 Z=0
    g9: GeomPoint X=-5.41644 Y=0.955065 Z=0
    g10: ArcOfCircle CenterX=-6.59821 CenterY=1.16344 CenterZ=0 NormalX=0 NormalY=0 NormalZ=1 AngleXU=0 Radius=1.2 StartAngle=2.96706 EndAngle=6.10865
    g11: ArcOfCircle CenterX=4e-16 CenterY=-2e-16 CenterZ=0 NormalX=0 NormalY=0 NormalZ=1 AngleXU=0 Radius=7.9 StartAngle=2.26893 EndAngle=2.96706
    g12: ArcOfCircle CenterX=-3e-16 CenterY=-2e-16 CenterZ=0 NormalX=0 NormalY=0 NormalZ=1 AngleXU=0 Radius=5.5 StartAngle=2.26893 EndAngle=2.96706
    g13: LineSegment [constr] StartX=4e-16 StartY=-2e-16 StartZ=0 EndX=6.29932 EndY=7.50724 EndZ=0
    g14: LineSegment [constr] StartX=-3e-16 StartY=-2e-16 StartZ=0 EndX=9.65112 EndY=1.70175 EndZ=0
    g15: LineSegment [constr] StartX=0 StartY=0 StartZ=0 EndX=3.3518 EndY=-9.20899 EndZ=0
    g16: LineSegment [constr] StartX=0 StartY=0 StartZ=0 EndX=-3.3518 EndY=-9.20899 EndZ=0
    g17: GeomPoint X=5.07802 Y=6.05175 Z=0
    g18: GeomPoint X=3.53533 Y=4.21324 Z=0
    g19: GeomPoint X=5.41644 Y=0.955065 Z=0
    g20: GeomPoint X=7.77998 Y=1.37182 Z=0
    g21: GeomPoint X=-1.88111 Y=-5.16831 Z=0
    g22: GeomPoint X=-2.70196 Y=-7.42357 Z=0
    g23: GeomPoint X=1.88111 Y=-5.16831 Z=0
    g24: GeomPoint X=2.70196 Y=-7.42357 Z=0
    g25: ArcOfCircle CenterX=4.30668 CenterY=5.1325 CenterZ=0 NormalX=0 NormalY=0 NormalZ=1 AngleXU=0 Radius=1.2 StartAngle=0.872665 EndAngle=4.01426
    g26: ArcOfCircle CenterX=6.59821 CenterY=1.16344 CenterZ=0 NormalX=0 NormalY=0 NormalZ=1 AngleXU=0 Radius=1.2 StartAngle=3.31613 EndAngle=6.45772
    g27: ArcOfCircle CenterX=0 CenterY=0 CenterZ=0 NormalX=0 NormalY=0 NormalZ=1 AngleXU=0 Radius=7.9 StartAngle=0.174533 EndAngle=0.872665
    g28: ArcOfCircle CenterX=2e-16 CenterY=3e-16 CenterZ=0 NormalX=0 NormalY=0 NormalZ=1 AngleXU=0 Radius=5.5 StartAngle=0.174533 EndAngle=0.872665
    g29: ArcOfCircle CenterX=-2.29153 CenterY=-6.29594 CenterZ=0 NormalX=0 NormalY=0 NormalZ=1 AngleXU=0 Radius=1.2 StartAngle=1.22173 EndAngle=4.36332
    g30: ArcOfCircle CenterX=2.29153 CenterY=-6.29594 CenterZ=0 NormalX=0 NormalY=0 NormalZ=1 AngleXU=0 Radius=1.2 StartAngle=5.06145 EndAngle=8.20305
    g31: ArcOfCircle CenterX=-8e-16 CenterY=1.1e-15 CenterZ=0 NormalX=0 NormalY=0 NormalZ=1 AngleXU=0 Radius=7.9 StartAngle=4.36332 EndAngle=5.06145
    g32: ArcOfCircle CenterX=-2.6e-15 CenterY=1e-16 CenterZ=0 NormalX=0 NormalY=0 NormalZ=1 AngleXU=0 Radius=5.5 StartAngle=4.36332 EndAngle=5.06145
  constraints (84):
    c: Diameter(g0) = 15.8
    c: Coincident(g0,g-1)
    c: Diameter(g1) = 11
    c: Coincident(g1,g0)
    c: Diameter(g2) = 6.6
    c: Coincident(g2,g0)
    c: Coincident(g3,g0)
    c: PointOnObject(g3,g-3)
    c: Angle(g-2,g3) = 0.698132
    c: Coincident(g4,g0)
    c: PointOnObject(g4,g-3)
    c: Angle(g3,g4) = 0.698132
    c: PointOnObject(g5,g0)
    c: PointOnObject(g5,g3)
    c: PointOnObject(g6,g1)
    c: PointOnObject(g6,g3)
    c: Coincident(g7,g5)
    c: Coincident(g7,g6)
    c: PointOnObject(g7,g3)
    c: PointOnObject(g8,g0)
    c: PointOnObject(g9,g1)
    c: PointOnObject(g9,g4)
    c: PointOnObject(g8,g4)
    c: Coincident(g10,g8)
    c: Coincident(g10,g9)
    c: PointOnObject(g10,g4)
    c: Equal(g0,g11)
    c: Coincident(g11,g5)
    c: Coincident(g11,g8)
    c: Equal(g12,g1)
    c: Coincident(g12,g6)
    c: Coincident(g12,g9)
    c: Coincident(g13,g11)
    c: PointOnObject(g13,g-3)
    c: Coincident(g14,g12)
    c: PointOnObject(g14,g-3)
    c: Angle(g13,g-2) = 0.698132
    c: Angle(g14,g13) = 0.698132
    c: Coincident(g15,g0)
    c: PointOnObject(g15,g-3)
    c: Coincident(g16,g0)
    c: PointOnObject(g16,g-3)
    c: Angle(g-2,g15) = 0.349066
    c: Angle(g16,g15) = 0.698132
    c: PointOnObject(g17,g13)
    c: PointOnObject(g18,g13)
    c: PointOnObject(g19,g14)
    c: PointOnObject(g20,g14)
    c: PointOnObject(g17,g0)
    c: PointOnObject(g18,g1)
    c: PointOnObject(g19,g1)
    c: PointOnObject(g20,g0)
    c: PointOnObject(g21,g16)
    c: PointOnObject(g22,g16)
    c: PointOnObject(g23,g15)
    c: PointOnObject(g24,g15)
    c: PointOnObject(g24,g0)
    c: PointOnObject(g23,g1)
    c: PointOnObject(g21,g1)
    c: PointOnObject(g22,g0)
    c: Coincident(g25,g17)
    c: Coincident(g25,g18)
    c: Coincident(g26,g19)
    c: Coincident(g26,g20)
    c: PointOnObject(g26,g14)
    c: PointOnObject(g25,g13)
    c: Coincident(g27,g17)
    c: Coincident(g27,g20)
    c: Equal(g0,g27)
    c: Coincident(g28,g18)
    c: Coincident(g28,g19)
    c: Equal(g28,g1)
    c: Coincident(g29,g21)
    c: Coincident(g29,g22)
    c: Coincident(g30,g24)
    c: Coincident(g30,g23)
    c: PointOnObject(g30,g15)
    c: PointOnObject(g29,g16)
    c: Coincident(g32,g23)
    c: Coincident(g32,g21)
    c: Coincident(g31,g22)
    c: Coincident(g31,g24)
    c: Equal(g32,g1)
    c: Equal(g31,g0)
FEATURE [PartDesign::Pocket] Pocket022
  BaseFeature = -> Pocket021
  Direction = (0,0,1)
  Length = 3.5
  Length2 = 5
  Profile = -> Sketch035
  ReferenceAxis = -> Sketch035 [N_Axis]
  SideType = 0
  Suppressed = false
  Type = 0
  Type2 = 0
FEATURE [Sketcher::SketchObject] Sketch036
  ArcFitTolerance = 1e-06
  AttachmentSupport = -> [Pocket022]
  ExternalTypes = [0]
  FullyConstrained = true
  MakeInternals = false
  MapMode = 5
  Placement = pos=(0,0,3.5) rot=(0,0,1;0rad)
  _ExternalGeoVersion = 0
  sketch-geometry (1):
    g0: Circle CenterX=0 CenterY=0 CenterZ=0 NormalX=0 NormalY=0 NormalZ=1 AngleXU=0 Radius=4.1
  constraints (2):
    c: Diameter(g0) = 8.2
    c: Coincident(g0,g-1)
FEATURE [PartDesign::Pocket] Pocket023
  BaseFeature = -> Pocket022
  Direction = (0,0,-1)
  Length = 1.4
  Length2 = 5
  Profile = -> Sketch036
  ReferenceAxis = -> Sketch036 [N_Axis]
  SideType = 0
  Suppressed = false
  Type = 0
  Type2 = 0
FEATURE [PartDesign::Body] Body011  label="EndCap_Top001"
  AllowCompound = false
  Group = -> [Sketch030,Pad011,Sketch031,Pad012,Sketch032,Pocket019,Sketch033,Pocket020,Fillet010,Sketch034,Pocket021,Sketch035,Pocket022,Sketch036,Pocket023]
  Origin = -> Origin023
  Placement = pos=(2.39184e-06,1e-05,139) rot=(0,1.00436,0;3.14159rad)
  Tip = -> Pocket023
FEATURE [PartDesign::SubShapeBinder] Binder008
  BindCopyOnChange = 0
  BindMode = 0
  ClaimChildren = false
  Context = -> Assembly [Body014.Binder008.]
  Fuse = false
  MakeFace = true
  OffsetFill = false
  OffsetIntersection = false
  OffsetJoinType = 0
  OffsetOpenResult = false
  PartialLoad = false
  Relative = true
  Support = -> [Body013[Pocket029.Edge61,Pocket029.Edge58,Pocket029.Edge62,Pocket029.Edge60,Pocket029.Edge59]]
  _Version = 2
FEATURE [PartDesign::SubShapeBinder] Binder009
  BindCopyOnChange = 0
  BindMode = 0
  ClaimChildren = false
  Context = -> Assembly [Body014.Binder009.]
  Fuse = false
  MakeFace = true
  OffsetFill = false
  OffsetIntersection = false
  OffsetJoinType = 0
  OffsetOpenResult = false
  PartialLoad = false
  Refine = true
  Relative = true
  Support = -> [Body013[Pocket029.Edge51,Pocket029.Edge56,Pocket029.Edge55,Pocket029.Edge53,Pocket029.Edge42,Pocket029.Edge37,Pocket029.Edge39,Pocket029.Edge41]]
  _Version = 2
FEATURE [App::Point] Origin029
  Role = Origin
FEATURE [App::Point] Origin030
  Role = Origin
FEATURE [PartDesign::Pad] Pad016
  Direction = (1.74533e-07,-4e-16,1)
  Length = 0.25
  Length2 = 10
  Profile = -> Binder008
  SideType = 0
  Suppressed = false
  Type = 0
  Type2 = 0
FEATURE [PartDesign::Pocket] Pocket030
  BaseFeature = -> Pad016
  Direction = (-1.74533e-07,0,-1)
  Length = 5
  Length2 = 5
  Profile = -> Binder009
  Reversed = true
  SideType = 0
  Suppressed = false
  Type = 1
  Type2 = 0
FEATURE [PartDesign::Body] Body014  label="MeshMask_Bottom"
  AllowCompound = false
  Group = -> [Binder008,Pad016,Binder009,Pocket030]
  Origin = -> Origin028
  Placement = pos=(0,0,-214.8) rot=(0,0,1;0rad)
  Tip = -> Pocket030
FEATURE [Assembly::AssemblyObject] Assembly
  Group = -> [Joints,Body002,Body012,Body006,Body004,Body008,Body001,Body,Body007,Body014,Body005,Body009,Exploded_Views,Exploded_View,Move,Move001,Move002,Move003,Move004,Move005,Move006,Move007,Move008,HexBolt,HexBolt001,HexBolt002,Move009,HexBolt003,HexBolt004,HexBolt005,Move010]
  Origin = -> Origin008
  Type = Assembly
FEATURE [Sketcher::SketchObject] Sketch037  label="22mmCircle003"
  ArcFitTolerance = 1e-06
  AttachmentSupport = -> [XY_Plane014]
  ExternalTypes = [0]
  FullyConstrained = true
  MakeInternals = false
  MapMode = 5
  _ExternalGeoVersion = 0
  sketch-geometry (1):
    g0: Circle CenterX=0 CenterY=0 CenterZ=0 NormalX=0 NormalY=0 NormalZ=1 AngleXU=0 Radius=11
  constraints (2):
    c: Diameter(g0) = 22
    c: Coincident(g0,g-1)
FEATURE [PartDesign::Pad] Pad014
  Direction = (0,0,1)
  Length = 8.5
  Length2 = 10
  Profile = -> Sketch037
  ReferenceAxis = -> Sketch037 [N_Axis]
  SideType = 0
  Suppressed = false
  Type = 0
  Type2 = 0
FEATURE [Sketcher::SketchObject] Sketch038
  ArcFitTolerance = 1e-06
  AttachmentSupport = -> [Pad014]
  ExternalTypes = [0]
  FullyConstrained = true
  MakeInternals = false
  MapMode = 5
  Placement = pos=(0,0,8.5) rot=(0,0,1;0rad)
  _ExternalGeoVersion = 0
  sketch-geometry (1):
    g0: Circle CenterX=0 CenterY=0 CenterZ=0 NormalX=0 NormalY=0 NormalZ=1 AngleXU=0 Radius=9.85
  constraints (2):
    c: Diameter(g0) = 19.7
    c: Coincident(g0,g-1)
FEATURE [PartDesign::Pad] Pad015
  BaseFeature = -> Pad014
  Direction = (0,0,1)
  Length = 2.5
  Length2 = 10
  Profile = -> Sketch038
  ReferenceAxis = -> Sketch038 [N_Axis]
  SideType = 0
  Suppressed = false
  Type = 0
  Type2 = 0
FEATURE [Sketcher::SketchObject] Sketch039
  ArcFitTolerance = 1e-06
  AttachmentSupport = -> [Pad015]
  ExternalTypes = [0]
  FullyConstrained = true
  MakeInternals = false
  MapMode = 5
  Placement = pos=(0,0,11) rot=(0,0,1;0rad)
  _ExternalGeoVersion = 0
  sketch-geometry (1):
    g0: Circle CenterX=0 CenterY=0 CenterZ=0 NormalX=0 NormalY=0 NormalZ=1 AngleXU=0 Radius=9
  constraints (2):
    c: Diameter(g0) = 18
    c: Coincident(g0,g-1)
FEATURE [PartDesign::Pocket] Pocket025
  BaseFeature = -> Pad015
  Direction = (0,0,-1)
  Length = 7.5
  Length2 = 5
  Profile = -> Sketch039
  ReferenceAxis = -> Sketch039 [N_Axis]
  SideType = 0
  Suppressed = false
  Type = 0
  Type2 = 0
FEATURE [Sketcher::SketchObject] Sketch040  label="BoltHoles_outer003"
  ArcFitTolerance = 1e-06
  AttachmentSupport = -> [Pocket025]
  ExternalGeometry = -> [Pocket025]
  ExternalTypes = [0]
  FullyConstrained = true
  MakeInternals = false
  MapMode = 5
  Placement = pos=(0,0,0) rot=(1,0,0;3.14159rad)
  _ExternalGeoVersion = 0
  sketch-geometry (5):
    g0: Circle CenterX=0 CenterY=6.8 CenterZ=0 NormalX=0 NormalY=0 NormalZ=1 AngleXU=0 Radius=1.95
    g1: Circle CenterX=-5.88897 CenterY=-3.4 CenterZ=0 NormalX=0 NormalY=0 NormalZ=1 AngleXU=0 Radius=1.95
    g2: Circle CenterX=5.88897 CenterY=-3.4 CenterZ=0 NormalX=0 NormalY=0 NormalZ=1 AngleXU=0 Radius=1.95
    g3: LineSegment [constr] StartX=0 StartY=0 StartZ=0 EndX=5.88897 EndY=-3.4 EndZ=0
    g4: LineSegment [constr] StartX=-5.88897 StartY=-3.4 StartZ=0 EndX=0 EndY=0 EndZ=0
  constraints (13):
    c: Diameter(g0) = 3.9
    c: PointOnObject(g0,g-2)
    c: Diameter(g1) = 3.9
    c: Diameter(g2) = 3.9
    c: Distance(g-1,g0) = 6.8
    c: Distance(g-1,g1) = 6.8
    c: Distance(g-1,g2) = 6.8
    c: Coincident(g3,g-1)
    c: Coincident(g3,g2)
    c: Angle(g3,g-2) = 2.0944
    c: Coincident(g4,g1)
    c: Coincident(g4,g3)
    c: Angle(g-2,g4) = 2.0944
FEATURE [PartDesign::Pocket] Pocket026
  BaseFeature = -> Pocket025
  Direction = (0,0,1)
  Length = 1.5
  Length2 = 5
  Profile = -> Sketch040
  ReferenceAxis = -> Sketch040 [N_Axis]
  SideType = 0
  Suppressed = false
  Type = 0
  Type2 = 0
FEATURE [PartDesign::Fillet] Fillet011
  Base = -> Pocket026 [Edge2]
  BaseFeature = -> Pocket026
  Radius = 1.2
  SupportTransform = false
  Suppressed = false
  UseAllEdges = false
FEATURE [Sketcher::SketchObject] Sketch041  label="BoltHoles_inner003"
  ArcFitTolerance = 1e-06
  AttachmentSupport = -> [Fillet011]
  ExternalGeometry = -> [Fillet011]
  ExternalTypes = [0]
  FullyConstrained = true
  MakeInternals = false
  MapMode = 5
  Placement = pos=(0,0,1.5) rot=(1,0,0;3.14159rad)
  _ExternalGeoVersion = 0
  sketch-geometry (3):
    g0: Circle CenterX=-5.88897 CenterY=-3.4 CenterZ=0 NormalX=0 NormalY=0 NormalZ=1 AngleXU=0 Radius=1.1
    g1: Circle CenterX=0 CenterY=6.8 CenterZ=0 NormalX=0 NormalY=0 NormalZ=1 AngleXU=0 Radius=1.1
    g2: Circle CenterX=5.88897 CenterY=-3.4 CenterZ=0 NormalX=0 NormalY=0 NormalZ=1 AngleXU=0 Radius=1.1
  constraints (6):
    c: Diameter(g0) = 2.2
    c: Coincident(g0,g-4)
    c: Diameter(g1) = 2.2
    c: Coincident(g1,g-3)
    c: Diameter(g2) = 2.2
    c: Coincident(g2,g-5)
FEATURE [PartDesign::Pocket] Pocket027
  BaseFeature = -> Fillet011
  Direction = (0,0,1)
  Length = 2
  Length2 = 5
  Profile = -> Sketch041
  ReferenceAxis = -> Sketch041 [N_Axis]
  SideType = 0
  Suppressed = false
  Type = 0
  Type2 = 0
FEATURE [Sketcher::SketchObject] Sketch042  label="VentHoles003"
  ArcFitTolerance = 1e-06
  AttachmentSupport = -> [Pocket027]
  ExternalGeometry = -> [Pocket027]
  ExternalTypes = [0]
  FullyConstrained = true
  MakeInternals = false
  MapMode = 5
  Placement = pos=(0,0,0) rot=(1,0,0;3.14159rad)
  _ExternalGeoVersion = 0
  sketch-geometry (33):
    g0: Circle [constr] CenterX=0 CenterY=0 CenterZ=0 NormalX=0 NormalY=0 NormalZ=1 AngleXU=0 Radius=7.9
    g1: Circle [constr] CenterX=0 CenterY=0 CenterZ=0 NormalX=0 NormalY=0 NormalZ=1 AngleXU=0 Radius=5.5
    g2: Circle CenterX=0 CenterY=0 CenterZ=0 NormalX=0 NormalY=0 NormalZ=1 AngleXU=0 Radius=3.3
    g3: LineSegment [constr] StartX=0 StartY=0 StartZ=0 EndX=-6.29932 EndY=7.50724 EndZ=0
    g4: LineSegment [constr] StartX=0 StartY=0 StartZ=0 EndX=-9.65112 EndY=1.70175 EndZ=0
    g5: GeomPoint X=-5.07802 Y=6.05175 Z=0
    g6: GeomPoint X=-3.53533 Y=4.21324 Z=0
    g7: ArcOfCircle CenterX=-4.30668 CenterY=5.1325 CenterZ=0 NormalX=0 NormalY=0 NormalZ=1 AngleXU=0 Radius=1.2 StartAngle=5.41052 EndAngle=8.55211
    g8: GeomPoint X=-7.77998 Y=1.37182 Z=0
    g9: GeomPoint X=-5.41644 Y=0.955065 Z=0
    g10: ArcOfCircle CenterX=-6.59821 CenterY=1.16344 CenterZ=0 NormalX=0 NormalY=0 NormalZ=1 AngleXU=0 Radius=1.2 StartAngle=2.96706 EndAngle=6.10865
    g11: ArcOfCircle CenterX=4e-16 CenterY=-2e-16 CenterZ=0 NormalX=0 NormalY=0 NormalZ=1 AngleXU=0 Radius=7.9 StartAngle=2.26893 EndAngle=2.96706
    g12: ArcOfCircle CenterX=-3e-16 CenterY=-2e-16 CenterZ=0 NormalX=0 NormalY=0 NormalZ=1 AngleXU=0 Radius=5.5 StartAngle=2.26893 EndAngle=2.96706
    g13: LineSegment [constr] StartX=4e-16 StartY=-2e-16 StartZ=0 EndX=6.29932 EndY=7.50724 EndZ=0
    g14: LineSegment [constr] StartX=-3e-16 StartY=-2e-16 StartZ=0 EndX=9.65112 EndY=1.70175 EndZ=0
    g15: LineSegment [constr] StartX=0 StartY=0 StartZ=0 EndX=3.3518 EndY=-9.20899 EndZ=0
    g16: LineSegment [constr] StartX=0 StartY=0 StartZ=0 EndX=-3.3518 EndY=-9.20899 EndZ=0
    g17: GeomPoint X=5.07802 Y=6.05175 Z=0
    g18: GeomPoint X=3.53533 Y=4.21324 Z=0
    g19: GeomPoint X=5.41644 Y=0.955065 Z=0
    g20: GeomPoint X=7.77998 Y=1.37182 Z=0
    g21: GeomPoint X=-1.88111 Y=-5.16831 Z=0
    g22: GeomPoint X=-2.70196 Y=-7.42357 Z=0
    g23: GeomPoint X=1.88111 Y=-5.16831 Z=0
    g24: GeomPoint X=2.70196 Y=-7.42357 Z=0
    g25: ArcOfCircle CenterX=4.30668 CenterY=5.1325 CenterZ=0 NormalX=0 NormalY=0 NormalZ=1 AngleXU=0 Radius=1.2 StartAngle=0.872665 EndAngle=4.01426
    g26: ArcOfCircle CenterX=6.59821 CenterY=1.16344 CenterZ=0 NormalX=0 NormalY=0 NormalZ=1 AngleXU=0 Radius=1.2 StartAngle=3.31613 EndAngle=6.45772
    g27: ArcOfCircle CenterX=0 CenterY=0 CenterZ=0 NormalX=0 NormalY=0 NormalZ=1 AngleXU=0 Radius=7.9 StartAngle=0.174533 EndAngle=0.872665
    g28: ArcOfCircle CenterX=2e-16 CenterY=3e-16 CenterZ=0 NormalX=0 NormalY=0 NormalZ=1 AngleXU=0 Radius=5.5 StartAngle=0.174533 EndAngle=0.872665
    g29: ArcOfCircle CenterX=-2.29153 CenterY=-6.29594 CenterZ=0 NormalX=0 NormalY=0 NormalZ=1 AngleXU=0 Radius=1.2 StartAngle=1.22173 EndAngle=4.36332
    g30: ArcOfCircle CenterX=2.29153 CenterY=-6.29594 CenterZ=0 NormalX=0 NormalY=0 NormalZ=1 AngleXU=0 Radius=1.2 StartAngle=5.06145 EndAngle=8.20305
    g31: ArcOfCircle CenterX=-8e-16 CenterY=1.1e-15 CenterZ=0 NormalX=0 NormalY=0 NormalZ=1 AngleXU=0 Radius=7.9 StartAngle=4.36332 EndAngle=5.06145
    g32: ArcOfCircle CenterX=-2.6e-15 CenterY=1e-16 CenterZ=0 NormalX=0 NormalY=0 NormalZ=1 AngleXU=0 Radius=5.5 StartAngle=4.36332 EndAngle=5.06145
  constraints (84):
    c: Diameter(g0) = 15.8
    c: Coincident(g0,g-1)
    c: Diameter(g1) = 11
    c: Coincident(g1,g0)
    c: Diameter(g2) = 6.6
    c: Coincident(g2,g0)
    c: Coincident(g3,g0)
    c: PointOnObject(g3,g-3)
    c: Angle(g-2,g3) = 0.698132
    c: Coincident(g4,g0)
    c: PointOnObject(g4,g-3)
    c: Angle(g3,g4) = 0.698132
    c: PointOnObject(g5,g0)
    c: PointOnObject(g5,g3)
    c: PointOnObject(g6,g1)
    c: PointOnObject(g6,g3)
    c: Coincident(g7,g5)
    c: Coincident(g7,g6)
    c: PointOnObject(g7,g3)
    c: PointOnObject(g8,g0)
    c: PointOnObject(g9,g1)
    c: PointOnObject(g9,g4)
    c: PointOnObject(g8,g4)
    c: Coincident(g10,g8)
    c: Coincident(g10,g9)
    c: PointOnObject(g10,g4)
    c: Equal(g0,g11)
    c: Coincident(g11,g5)
    c: Coincident(g11,g8)
    c: Equal(g12,g1)
    c: Coincident(g12,g6)
    c: Coincident(g12,g9)
    c: Coincident(g13,g11)
    c: PointOnObject(g13,g-3)
    c: Coincident(g14,g12)
    c: PointOnObject(g14,g-3)
    c: Angle(g13,g-2) = 0.698132
    c: Angle(g14,g13) = 0.698132
    c: Coincident(g15,g0)
    c: PointOnObject(g15,g-3)
    c: Coincident(g16,g0)
    c: PointOnObject(g16,g-3)
    c: Angle(g-2,g15) = 0.349066
    c: Angle(g16,g15) = 0.698132
    c: PointOnObject(g17,g13)
    c: PointOnObject(g18,g13)
    c: PointOnObject(g19,g14)
    c: PointOnObject(g20,g14)
    c: PointOnObject(g17,g0)
    c: PointOnObject(g18,g1)
    c: PointOnObject(g19,g1)
    c: PointOnObject(g20,g0)
    c: PointOnObject(g21,g16)
    c: PointOnObject(g22,g16)
    c: PointOnObject(g23,g15)
    c: PointOnObject(g24,g15)
    c: PointOnObject(g24,g0)
    c: PointOnObject(g23,g1)
    c: PointOnObject(g21,g1)
    c: PointOnObject(g22,g0)
    c: Coincident(g25,g17)
    c: Coincident(g25,g18)
    c: Coincident(g26,g19)
    c: Coincident(g26,g20)
    c: PointOnObject(g26,g14)
    c: PointOnObject(g25,g13)
    c: Coincident(g27,g17)
    c: Coincident(g27,g20)
    c: Equal(g0,g27)
    c: Coincident(g28,g18)
    c: Coincident(g28,g19)
    c: Equal(g28,g1)
    c: Coincident(g29,g21)
    c: Coincident(g29,g22)
    c: Coincident(g30,g24)
    c: Coincident(g30,g23)
    c: PointOnObject(g30,g15)
    c: PointOnObject(g29,g16)
    c: Coincident(g32,g23)
    c: Coincident(g32,g21)
    c: Coincident(g31,g22)
    c: Coincident(g31,g24)
    c: Equal(g32,g1)
    c: Equal(g31,g0)
FEATURE [PartDesign::Pocket] Pocket028
  BaseFeature = -> Pocket027
  Direction = (0,0,1)
  Length = 3.5
  Length2 = 5
  Profile = -> Sketch042
  ReferenceAxis = -> Sketch042 [N_Axis]
  SideType = 0
  Suppressed = false
  Type = 0
  Type2 = 0
FEATURE [Sketcher::SketchObject] Sketch043
  ArcFitTolerance = 1e-06
  AttachmentSupport = -> [Pocket028]
  ExternalTypes = [0]
  FullyConstrained = true
  MakeInternals = false
  MapMode = 5
  Placement = pos=(0,0,3.5) rot=(0,0,1;0rad)
  _ExternalGeoVersion = 0
  sketch-geometry (1):
    g0: Circle CenterX=0 CenterY=0 CenterZ=0 NormalX=0 NormalY=0 NormalZ=1 AngleXU=0 Radius=4.1
  constraints (2):
    c: Diameter(g0) = 8.2
    c: Coincident(g0,g-1)
FEATURE [PartDesign::Pocket] Pocket029
  BaseFeature = -> Pocket028
  Direction = (0,0,-1)
  Length = 1.4
  Length2 = 5
  Profile = -> Sketch043
  ReferenceAxis = -> Sketch043 [N_Axis]
  SideType = 0
  Suppressed = false
  Type = 0
  Type2 = 0
FEATURE [PartDesign::Body] Body013  label="EndCap_Top002"
  AllowCompound = false
  Group = -> [Sketch037,Pad014,Sketch038,Pad015,Sketch039,Pocket025,Sketch040,Pocket026,Fillet011,Sketch041,Pocket027,Sketch042,Pocket028,Sketch043,Pocket029]
  Origin = -> Origin027
  Placement = pos=(2.39184e-06,1e-05,139) rot=(0,1.00436,0;3.14159rad)
  Tip = -> Pocket029
